# Revit family: 926-00-001-DN80-1800
name_source: partatom
category: Pipe Accessories
units: mm (PartAtom-declared; Revit-internal decimal feet)

## family parameters
Always vertical = Yes
Cut with Voids When Loaded = No
Part Type = Valve - Breaks Into
Round Connector Dimension = Use Diameter
Shared = No
Work Plane-Based = No

## types (33) — shared parameters
Description_ = AVK DBL. ECC. BUTTERFLY VALVE, FLANGED, AWWA SHORT, PN10/16
Search_table = 926-00-001-DN80-1800
URL_product_pages = https://www.avkvalves.com
zero-valued in all types: Default Elevation

## per-type parameters (varying)
- DN080_PN10/16: A=127 mm; B=110 mm; Body_T=8 mm  [stored 0.0262467 ft]; Body_end_shaft_R=60 mm; Body_rib_L=20 mm  [stored 0.0656168 ft]; Body_rib_W=12 mm  [stored 0.0393701 ft]; Body_shaft_R1=58 mm; Body_shaft_R2=16 mm  [stored 0.0524934 ft]; Body_shaft_R2_T=7 mm  [stored 0.0229659 ft]; Body_shaft_R3=21 mm  [stored 0.0688976 ft]; Body_shaft_R3_T=4 mm  [stored 0.0131234 ft]; Bore_R=40 mm; C=185 mm; D=9 mm  [stored 0.0295276 ft]; DN=80 mm; DN080_PN10/16=926-A10-12-020140100000; DN1000_PN10=926-A10-12-020140100000; DN1000_PN16=926-080-12-020140100000; DN100_PN10/16=926-100-12-020140100000; DN150_PN10/16=926-150-12-020040100000; DN200_PN10=926-200-12-010040100000; DN200_PN16=926-200-12-020040100000; DN250_PN10=926-250-12-010040100000; DN250_PN16=926-250-12-020040100000; DN300_PN10=926-300-12-010040100000; DN300_PN16=926-300-12-020040100000; DN350_PN10=926-350-12-010040100000; DN350_PN16=926-350-12-020040100000; DN400_PN10=926-400-12-010040100000; DN400_PN16=926-400-12-020040100000; DN500_PN10=926-500-12-010040100000; DN500_PN16=926-500-12-020040100000; DN600_PN10=926-600-12-020040100000; DN600_PN16=926-600-12-020040100000; DN700_PN10=926-700-12-020040100000; DN700_PN16=926-700-12-020040100000; E=18 mm  [stored 0.0590551 ft]; FL_R=72 mm; FL_T=8 mm  [stored 0.0262467 ft]; Hole_R=5 mm  [stored 0.0164042 ft]; L=3 mm  [stored 0.00984252 ft]; PCD=160 mm; Raised_R=66 mm; Raised_dis=2 mm  [stored 0.00656168 ft]; Retainer=16 mm  [stored 0.0524934 ft]; Rib_R=5 mm  [stored 0.0164042 ft]; Rib_T=4 mm  [stored 0.0131234 ft]; Rib_shaft=21 mm  [stored 0.0688976 ft]; Rib_shaft1=16 mm  [stored 0.0524934 ft]; Seal_R=16 mm  [stored 0.0524934 ft]; Slot_T=14 mm  [stored 0.0459318 ft]; Slot_dim1=15 mm  [stored 0.0492126 ft]; Slt=9 mm  [stored 0.0295276 ft]; Stem_R=7 mm  [stored 0.0229659 ft]; Top _Flange_dim1=12 mm  [stored 0.0393701 ft]; Top _Flange_dim2=8 mm  [stored 0.0262467 ft]; Top_Flange1=9 mm  [stored 0.0295276 ft]; Top_Flange_R=45 mm; Top_Flange_R_T=28 mm  [stored 0.0918635 ft]; Top_Flange_T=7 mm  [stored 0.0229659 ft]; Top_Rib=5 mm  [stored 0.0164042 ft]; Wedge=98 mm; bottom_Shaft_R=25 mm  [stored 0.082021 ft]; bottom_Shaft_T=5 mm  [stored 0.0164042 ft]; bottom_support_T=24 mm  [stored 0.0787402 ft]; logo=50 mm; rib_Loctn=8 mm  [stored 0.0262467 ft]; total_FL_legth=124 mm
- DN100_PN10/16: A=127 mm; B=130 mm; Body_T=10 mm  [stored 0.0328084 ft]; Body_end_shaft_R=60 mm; Body_rib_L=25 mm  [stored 0.082021 ft]; Body_rib_W=15 mm  [stored 0.0492126 ft]; Body_shaft_R1=58 mm; Body_shaft_R2=20 mm  [stored 0.0656168 ft]; Body_shaft_R2_T=9 mm  [stored 0.0295276 ft]; Body_shaft_R3=26 mm; Body_shaft_R3_T=5 mm  [stored 0.0164042 ft]; Bore_R=50 mm; C=202 mm; D=11 mm  [stored 0.0360892 ft]; DN=100 mm; DN080_PN10/16=926-080-00-020140100000; DN1000_PN10=926-A10-00-010020100000; DN1000_PN16=926-A10-00-020020100000; DN100_PN10/16=926-100-00-020140100000; DN1200_PN10=926-A12-00-010020100000; DN1200_PN16=926-A12-00-020020100000; DN1500_PN10=926-A15-00-010020100000; DN1500_PN16=926-A15-00-020020100000; DN150_PN10/16=926-150-00-020040100000; DN1800_PN10=926-A18-00-010020100000; DN1800_PN16=926-A18-00-020020100000; DN200_PN10=926-200-00-010040100000; DN200_PN16=926-200-00-020040100000; DN250_PN10=926-250-00-010040100000; DN250_PN16=926-250-00-020040100000; DN300_PN10=926-300-00-010040100000; DN300_PN16=926-300-00-020040100000; DN350_PN10=926-350-00-010040100000; DN350_PN16=926-350-00-020040100000; DN400_PN10=926-400-00-010040100000; DN400_PN16=926-400-00-020040100000; DN500_PN10=926-500-00-010040100000; DN500_PN16=926-500-00-020040100000; DN600_PN10=926-600-00-010040100000; DN600_PN16=926-600-00-020040100000; DN700_PN10=926-700-00-010020100000; DN700_PN16=926-700-00-020020100000; DN750_PN10=926-750-00-010020100000; DN750_PN16=926-750-00-020020100000; DN800_PN10=926-800-00-010020100000; DN800_PN16=926-800-00-020020100000; DN900_PN10=926-900-00-010020100000; DN900_PN16=926-900-00-020020100000; E=20 mm  [stored 0.0656168 ft]; FL_R=81 mm; FL_T=8 mm  [stored 0.0262467 ft]; Hole_R=6 mm  [stored 0.019685 ft]; L=3 mm  [stored 0.00984252 ft]; PCD=180 mm; Raised_R=78 mm; Raised_dis=2 mm  [stored 0.00656168 ft]; Retainer=16 mm  [stored 0.0524934 ft]; Rib_R=6 mm  [stored 0.019685 ft]; Rib_T=4 mm  [stored 0.0131234 ft]; Rib_shaft=26 mm; Rib_shaft1=20 mm  [stored 0.0656168 ft]; Seal_R=16 mm  [stored 0.0524934 ft]; Slot_T=14 mm  [stored 0.0459318 ft]; Slot_dim1=15 mm  [stored 0.0492126 ft]; Slt=11 mm  [stored 0.0360892 ft]; Stem_R=8 mm  [stored 0.0262467 ft]; Top _Flange_dim1=15 mm  [stored 0.0492126 ft]; Top _Flange_dim2=10 mm  [stored 0.0328084 ft]; Top_Flange1=15 mm  [stored 0.0492126 ft]; Top_Flange_R=63 mm; Top_Flange_R_T=28 mm  [stored 0.0918635 ft]; Top_Flange_T=9 mm  [stored 0.0295276 ft]; Top_Rib=6 mm  [stored 0.019685 ft]; Wedge=98 mm; bottom_Shaft_R=31 mm  [stored 0.101706 ft]; bottom_Shaft_T=6 mm  [stored 0.019685 ft]; bottom_support_T=30 mm  [stored 0.0984252 ft]; logo=62 mm; rib_Loctn=10 mm  [stored 0.0328084 ft]; total_FL_legth=124 mm
- DN200_PN10: A=152 mm; B=200 mm; Body_T=12 mm  [stored 0.0393701 ft]; Body_end_shaft_R=71 mm; Body_rib_L=52 mm; Body_rib_W=22 mm  [stored 0.0721785 ft]; Body_shaft_R1=64 mm; Body_shaft_R2=42 mm; Body_shaft_R2_T=18 mm  [stored 0.0590551 ft]; Body_shaft_R3=54 mm; Body_shaft_R3_T=10 mm  [stored 0.0328084 ft]; Bore_R=100 mm; C=320 mm; D=22 mm  [stored 0.0721785 ft]; DN=200 mm; DN080_PN10/16=926-080-00-020140100000; DN1000_PN10=926-A10-00-010020100000; DN1000_PN16=926-A10-00-020020100000; DN100_PN10/16=926-100-00-020140100000; DN1200_PN10=926-A12-00-010020100000; DN1200_PN16=926-A12-00-020020100000; DN1500_PN10=926-A15-00-010020100000; DN1500_PN16=926-A15-00-020020100000; DN150_PN10/16=926-150-00-020040100000; DN1800_PN10=926-A18-00-010020100000; DN1800_PN16=926-A18-00-020020100000; DN200_PN10=926-200-00-010040100000; DN200_PN16=926-200-00-020040100000; DN250_PN10=926-250-00-010040100000; DN250_PN16=926-250-00-020040100000; DN300_PN10=926-300-00-010040100000; DN300_PN16=926-300-00-020040100000; DN350_PN10=926-350-00-010040100000; DN350_PN16=926-350-00-020040100000; DN400_PN10=926-400-00-010040100000; DN400_PN16=926-400-00-020040100000; DN500_PN10=926-500-00-010040100000; DN500_PN16=926-500-00-020040100000; DN600_PN10=926-600-00-010040100000; DN600_PN16=926-600-00-020040100000; DN700_PN10=926-700-00-010020100000; DN700_PN16=926-700-00-020020100000; DN750_PN10=926-750-00-010020100000; DN750_PN16=926-750-00-020020100000; DN800_PN10=926-800-00-010020100000; DN800_PN16=926-800-00-020020100000; DN900_PN10=926-900-00-010020100000; DN900_PN16=926-900-00-020020100000; E=30 mm  [stored 0.0984252 ft]; FL_R=133 mm; FL_T=20 mm  [stored 0.0656168 ft]; Hole_R=12 mm  [stored 0.0393701 ft]; L=5 mm  [stored 0.0164042 ft]; PCD=295 mm; Raised_R=133 mm; Raised_dis=3 mm  [stored 0.00984252 ft]; Retainer=16 mm  [stored 0.0524934 ft]; Rib_R=11 mm  [stored 0.0360892 ft]; Rib_T=11 mm  [stored 0.0360892 ft]; Rib_shaft=54 mm; Rib_shaft1=42 mm; Seal_R=16 mm  [stored 0.0524934 ft]; Slot_T=20 mm  [stored 0.0656168 ft]; Slot_dim1=21 mm  [stored 0.0688976 ft]; Slt=22 mm  [stored 0.0721785 ft]; Stem_R=17 mm  [stored 0.0557743 ft]; Top _Flange_dim1=31 mm  [stored 0.101706 ft]; Top _Flange_dim2=20 mm  [stored 0.0656168 ft]; Top_Flange1=22 mm  [stored 0.0721785 ft]; Top_Flange_R=75 mm; Top_Flange_R_T=40 mm; Top_Flange_T=18 mm  [stored 0.0590551 ft]; Top_Rib=11 mm  [stored 0.0360892 ft]; Wedge=117 mm; bottom_Shaft_R=65 mm; bottom_Shaft_T=9 mm  [stored 0.0295276 ft]; bottom_support_T=62 mm; logo=114 mm; rib_Loctn=21 mm  [stored 0.0688976 ft]; total_FL_legth=148 mm
- DN150_PN10/16: A=127 mm; B=170 mm; Body_T=12 mm  [stored 0.0393701 ft]; Body_end_shaft_R=60 mm; Body_rib_L=32 mm  [stored 0.104987 ft]; Body_rib_W=20 mm  [stored 0.0656168 ft]; Body_shaft_R1=57 mm; Body_shaft_R2=26 mm; Body_shaft_R2_T=14 mm  [stored 0.0459318 ft]; Body_shaft_R3=33 mm  [stored 0.108268 ft]; Body_shaft_R3_T=7 mm  [stored 0.0229659 ft]; Bore_R=75 mm; C=280 mm; D=17 mm  [stored 0.0557743 ft]; DN=150 mm; DN080_PN10/16=926-080-00-020140100000; DN1000_PN10=926-A10-00-010020100000; DN1000_PN16=926-A10-00-020020100000; DN100_PN10/16=926-100-00-020140100000; DN1200_PN10=926-A12-00-010020100000; DN1200_PN16=926-A12-00-020020100000; DN1500_PN10=926-A15-00-010020100000; DN1500_PN16=926-A15-00-020020100000; DN150_PN10/16=926-150-00-020040100000; DN1800_PN10=926-A18-00-010020100000; DN1800_PN16=926-A18-00-020020100000; DN200_PN10=926-200-00-010040100000; DN200_PN16=926-200-00-020040100000; DN250_PN10=926-250-00-010040100000; DN250_PN16=926-250-00-020040100000; DN300_PN10=926-300-00-010040100000; DN300_PN16=926-300-00-020040100000; DN350_PN10=926-350-00-010040100000; DN350_PN16=926-350-00-020040100000; DN400_PN10=926-400-00-010040100000; DN400_PN16=926-400-00-020040100000; DN500_PN10=926-500-00-010040100000; DN500_PN16=926-500-00-020040100000; DN600_PN10=926-600-00-010040100000; DN600_PN16=926-600-00-020040100000; DN700_PN10=926-700-00-010020100000; DN700_PN16=926-700-00-020020100000; DN750_PN10=926-750-00-010020100000; DN750_PN16=926-750-00-020020100000; DN800_PN10=926-800-00-010020100000; DN800_PN16=926-800-00-020020100000; DN900_PN10=926-900-00-010020100000; DN900_PN16=926-900-00-020020100000; E=27 mm  [stored 0.0885827 ft]; FL_R=108 mm; FL_T=10 mm  [stored 0.0328084 ft]; Hole_R=8 mm  [stored 0.0262467 ft]; L=3 mm  [stored 0.00984252 ft]; PCD=240 mm; Raised_R=106 mm; Raised_dis=2 mm  [stored 0.00656168 ft]; Retainer=17 mm  [stored 0.0557743 ft]; Rib_R=9 mm  [stored 0.0295276 ft]; Rib_T=5 mm  [stored 0.0164042 ft]; Rib_shaft=33 mm  [stored 0.108268 ft]; Rib_shaft1=26 mm; Seal_R=17 mm  [stored 0.0557743 ft]; Slot_T=22 mm  [stored 0.0721785 ft]; Slot_dim1=18 mm  [stored 0.0590551 ft]; Slt=17 mm  [stored 0.0557743 ft]; Stem_R=13 mm  [stored 0.0426509 ft]; Top _Flange_dim1=19 mm  [stored 0.062336 ft]; Top _Flange_dim2=14 mm  [stored 0.0459318 ft]; Top_Flange1=18 mm  [stored 0.0590551 ft]; Top_Flange_R=63 mm; Top_Flange_R_T=44 mm; Top_Flange_T=14 mm  [stored 0.0459318 ft]; Top_Rib=9 mm  [stored 0.0295276 ft]; Wedge=98 mm; bottom_Shaft_R=40 mm; bottom_Shaft_T=8 mm  [stored 0.0262467 ft]; bottom_support_T=38 mm  [stored 0.124672 ft]; logo=89 mm; rib_Loctn=13 mm  [stored 0.0426509 ft]; total_FL_legth=124 mm
- DN200_PN16: A=152 mm; B=200 mm; Body_T=14 mm  [stored 0.0459318 ft]; Body_end_shaft_R=71 mm; Body_rib_L=52 mm; Body_rib_W=22 mm  [stored 0.0721785 ft]; Body_shaft_R1=64 mm; Body_shaft_R2=42 mm; Body_shaft_R2_T=18 mm  [stored 0.0590551 ft]; Body_shaft_R3=54 mm; Body_shaft_R3_T=10 mm  [stored 0.0328084 ft]; Bore_R=100 mm; C=320 mm; D=22 mm  [stored 0.0721785 ft]; DN=200 mm; DN080_PN10/16=926-080-00-020140100000; DN1000_PN10=926-A10-00-010020100000; DN1000_PN16=926-A10-00-020020100000; DN100_PN10/16=926-100-00-020140100000; DN1200_PN10=926-A12-00-010020100000; DN1200_PN16=926-A12-00-020020100000; DN1500_PN10=926-A15-00-010020100000; DN1500_PN16=926-A15-00-020020100000; DN150_PN10/16=926-150-00-020040100000; DN1800_PN10=926-A18-00-010020100000; DN1800_PN16=926-A18-00-020020100000; DN200_PN10=926-200-00-010040100000; DN200_PN16=926-200-00-020040100000; DN250_PN10=926-250-00-010040100000; DN250_PN16=926-250-00-020040100000; DN300_PN10=926-300-00-010040100000; DN300_PN16=926-300-00-020040100000; DN350_PN10=926-350-00-010040100000; DN350_PN16=926-350-00-020040100000; DN400_PN10=926-400-00-010040100000; DN400_PN16=926-400-00-020040100000; DN500_PN10=926-500-00-010040100000; DN500_PN16=926-500-00-020040100000; DN600_PN10=926-600-00-010040100000; DN600_PN16=926-600-00-020040100000; DN700_PN10=926-700-00-010020100000; DN700_PN16=926-700-00-020020100000; DN750_PN10=926-750-00-010020100000; DN750_PN16=926-750-00-020020100000; DN800_PN10=926-800-00-010020100000; DN800_PN16=926-800-00-020020100000; DN900_PN10=926-900-00-010020100000; DN900_PN16=926-900-00-020020100000; E=30 mm  [stored 0.0984252 ft]; FL_R=133 mm; FL_T=20 mm  [stored 0.0656168 ft]; Hole_R=12 mm  [stored 0.0393701 ft]; L=5 mm  [stored 0.0164042 ft]; PCD=295 mm; Raised_R=133 mm; Raised_dis=3 mm  [stored 0.00984252 ft]; Retainer=16 mm  [stored 0.0524934 ft]; Rib_R=11 mm  [stored 0.0360892 ft]; Rib_T=11 mm  [stored 0.0360892 ft]; Rib_shaft=54 mm; Rib_shaft1=42 mm; Seal_R=16 mm  [stored 0.0524934 ft]; Slot_T=20 mm  [stored 0.0656168 ft]; Slot_dim1=21 mm  [stored 0.0688976 ft]; Slt=22 mm  [stored 0.0721785 ft]; Stem_R=17 mm  [stored 0.0557743 ft]; Top _Flange_dim1=31 mm  [stored 0.101706 ft]; Top _Flange_dim2=20 mm  [stored 0.0656168 ft]; Top_Flange1=21 mm  [stored 0.0688976 ft]; Top_Flange_R=75 mm; Top_Flange_R_T=40 mm; Top_Flange_T=18 mm  [stored 0.0590551 ft]; Top_Rib=11 mm  [stored 0.0360892 ft]; Wedge=117 mm; bottom_Shaft_R=65 mm; bottom_Shaft_T=9 mm  [stored 0.0295276 ft]; bottom_support_T=62 mm; logo=116 mm; rib_Loctn=21 mm  [stored 0.0688976 ft]; total_FL_legth=148 mm
- DN250_PN10: A=203 mm; B=222 mm; Body_T=14 mm  [stored 0.0459318 ft]; Body_end_shaft_R=96 mm; Body_rib_L=56 mm; Body_rib_W=24 mm  [stored 0.0787402 ft]; Body_shaft_R1=88 mm; Body_shaft_R2=45 mm; Body_shaft_R2_T=22 mm  [stored 0.0721785 ft]; Body_shaft_R3=58 mm; Body_shaft_R3_T=12 mm  [stored 0.0393701 ft]; Bore_R=125 mm; C=340 mm; D=27 mm  [stored 0.0885827 ft]; DN=250 mm; DN080_PN10/16=926-080-00-020140100000; DN1000_PN10=926-A10-00-010020100000; DN1000_PN16=926-A10-00-020020100000; DN100_PN10/16=926-100-00-020140100000; DN1200_PN10=926-A12-00-010020100000; DN1200_PN16=926-A12-00-020020100000; DN1500_PN10=926-A15-00-010020100000; DN1500_PN16=926-A15-00-020020100000; DN150_PN10/16=926-150-00-020040100000; DN1800_PN10=926-A18-00-010020100000; DN1800_PN16=926-A18-00-020020100000; DN200_PN10=926-200-00-010040100000; DN200_PN16=926-200-00-020040100000; DN250_PN10=926-250-00-010040100000; DN250_PN16=926-250-00-020040100000; DN300_PN10=926-300-00-010040100000; DN300_PN16=926-300-00-020040100000; DN350_PN10=926-350-00-010040100000; DN350_PN16=926-350-00-020040100000; DN400_PN10=926-400-00-010040100000; DN400_PN16=926-400-00-020040100000; DN500_PN10=926-500-00-010040100000; DN500_PN16=926-500-00-020040100000; DN600_PN10=926-600-00-010040100000; DN600_PN16=926-600-00-020040100000; DN700_PN10=926-700-00-010020100000; DN700_PN16=926-700-00-020020100000; DN750_PN10=926-750-00-010020100000; DN750_PN16=926-750-00-020020100000; DN800_PN10=926-800-00-010020100000; DN800_PN16=926-800-00-020020100000; DN900_PN10=926-900-00-010020100000; DN900_PN16=926-900-00-020020100000; E=36 mm  [stored 0.11811 ft]; FL_R=158 mm; FL_T=22 mm  [stored 0.0721785 ft]; Hole_R=12 mm  [stored 0.0393701 ft]; L=5 mm  [stored 0.0164042 ft]; PCD=350 mm; Raised_R=160 mm; Raised_dis=3 mm  [stored 0.00984252 ft]; Retainer=16 mm  [stored 0.0524934 ft]; Rib_R=14 mm  [stored 0.0459318 ft]; Rib_T=13 mm  [stored 0.0426509 ft]; Rib_shaft=58 mm; Rib_shaft1=45 mm; Seal_R=16 mm  [stored 0.0524934 ft]; Slot_T=20 mm  [stored 0.0656168 ft]; Slot_dim1=6 mm  [stored 0.019685 ft]; Slt=27 mm  [stored 0.0885827 ft]; Stem_R=20 mm  [stored 0.0656168 ft]; Top _Flange_dim1=34 mm; Top _Flange_dim2=24 mm  [stored 0.0787402 ft]; Top_Flange1=21 mm  [stored 0.0688976 ft]; Top_Flange_R=75 mm; Top_Flange_R_T=40 mm; Top_Flange_T=22 mm  [stored 0.0721785 ft]; Top_Rib=14 mm  [stored 0.0459318 ft]; Wedge=156 mm; bottom_Shaft_R=70 mm; bottom_Shaft_T=10 mm  [stored 0.0328084 ft]; bottom_support_T=67 mm; logo=141 mm; rib_Loctn=22 mm  [stored 0.0721785 ft]; total_FL_legth=199 mm
- DN250_PN16: A=203 mm; B=222 mm; Body_T=4 mm  [stored 0.0131234 ft]; Body_end_shaft_R=96 mm; Body_rib_L=56 mm; Body_rib_W=24 mm  [stored 0.0787402 ft]; Body_shaft_R1=88 mm; Body_shaft_R2=45 mm; Body_shaft_R2_T=22 mm  [stored 0.0721785 ft]; Body_shaft_R3=58 mm; Body_shaft_R3_T=12 mm  [stored 0.0393701 ft]; Bore_R=125 mm; C=340 mm; D=27 mm  [stored 0.0885827 ft]; DN=250 mm; DN080_PN10/16=926-080-00-020140100000; DN1000_PN10=926-A10-00-010020100000; DN1000_PN16=926-A10-00-020020100000; DN100_PN10/16=926-100-00-020140100000; DN1200_PN10=926-A12-00-010020100000; DN1200_PN16=926-A12-00-020020100000; DN1500_PN10=926-A15-00-010020100000; DN1500_PN16=926-A15-00-020020100000; DN150_PN10/16=926-150-00-020040100000; DN1800_PN10=926-A18-00-010020100000; DN1800_PN16=926-A18-00-020020100000; DN200_PN10=926-200-00-010040100000; DN200_PN16=926-200-00-020040100000; DN250_PN10=926-250-00-010040100000; DN250_PN16=926-250-00-020040100000; DN300_PN10=926-300-00-010040100000; DN300_PN16=926-300-00-020040100000; DN350_PN10=926-350-00-010040100000; DN350_PN16=926-350-00-020040100000; DN400_PN10=926-400-00-010040100000; DN400_PN16=926-400-00-020040100000; DN500_PN10=926-500-00-010040100000; DN500_PN16=926-500-00-020040100000; DN600_PN10=926-600-00-010040100000; DN600_PN16=926-600-00-020040100000; DN700_PN10=926-700-00-010020100000; DN700_PN16=926-700-00-020020100000; DN750_PN10=926-750-00-010020100000; DN750_PN16=926-750-00-020020100000; DN800_PN10=926-800-00-010020100000; DN800_PN16=926-800-00-020020100000; DN900_PN10=926-900-00-010020100000; DN900_PN16=926-900-00-020020100000; E=36 mm  [stored 0.11811 ft]; FL_R=160 mm; FL_T=22 mm  [stored 0.0721785 ft]; Hole_R=11 mm  [stored 0.0360892 ft]; L=5 mm  [stored 0.0164042 ft]; PCD=355 mm; Raised_R=160 mm; Raised_dis=3 mm  [stored 0.00984252 ft]; Retainer=17 mm  [stored 0.0557743 ft]; Rib_R=14 mm  [stored 0.0459318 ft]; Rib_T=13 mm  [stored 0.0426509 ft]; Rib_shaft=58 mm; Rib_shaft1=45 mm; Seal_R=17 mm  [stored 0.0557743 ft]; Slot_T=20 mm  [stored 0.0656168 ft]; Slot_dim1=6 mm  [stored 0.019685 ft]; Slt=27 mm  [stored 0.0885827 ft]; Stem_R=20 mm  [stored 0.0656168 ft]; Top _Flange_dim1=34 mm; Top _Flange_dim2=24 mm  [stored 0.0787402 ft]; Top_Flange1=22 mm  [stored 0.0721785 ft]; Top_Flange_R=75 mm; Top_Flange_R_T=40 mm; Top_Flange_T=22 mm  [stored 0.0721785 ft]; Top_Rib=14 mm  [stored 0.0459318 ft]; Wedge=156 mm; bottom_Shaft_R=70 mm; bottom_Shaft_T=10 mm  [stored 0.0328084 ft]; bottom_support_T=67 mm; logo=131 mm; rib_Loctn=22 mm  [stored 0.0721785 ft]; total_FL_legth=199 mm
- DN300_PN10: A=203 mm; B=260 mm; Body_T=14 mm  [stored 0.0459318 ft]; Body_end_shaft_R=95 mm; Body_rib_L=60 mm; Body_rib_W=30 mm  [stored 0.0984252 ft]; Body_shaft_R1=86 mm; Body_shaft_R2=48 mm; Body_shaft_R2_T=22 mm  [stored 0.0721785 ft]; Body_shaft_R3=62 mm; Body_shaft_R3_T=12 mm  [stored 0.0393701 ft]; Bore_R=150 mm; C=390 mm; D=27 mm  [stored 0.0885827 ft]; DN=300 mm; DN080_PN10/16=926-080-00-020140100000; DN1000_PN10=926-A10-00-010020100000; DN1000_PN16=926-A10-00-020020100000; DN100_PN10/16=926-100-00-020140100000; DN1200_PN10=926-A12-00-010020100000; DN1200_PN16=926-A12-00-020020100000; DN1500_PN10=926-A15-00-010020100000; DN1500_PN16=926-A15-00-020020100000; DN150_PN10/16=926-150-00-020040100000; DN1800_PN10=926-A18-00-010020100000; DN1800_PN16=926-A18-00-020020100000; DN200_PN10=926-200-00-010040100000; DN200_PN16=926-200-00-020040100000; DN250_PN10=926-250-00-010040100000; DN250_PN16=926-250-00-020040100000; DN300_PN10=926-300-00-010040100000; DN300_PN16=926-300-00-020040100000; DN350_PN10=926-350-00-010040100000; DN350_PN16=926-350-00-020040100000; DN400_PN10=926-400-00-010040100000; DN400_PN16=926-400-00-020040100000; DN500_PN10=926-500-00-010040100000; DN500_PN16=926-500-00-020040100000; DN600_PN10=926-600-00-010040100000; DN600_PN16=926-600-00-020040100000; DN700_PN10=926-700-00-010020100000; DN700_PN16=926-700-00-020020100000; DN750_PN10=926-750-00-010020100000; DN750_PN16=926-750-00-020020100000; DN800_PN10=926-800-00-010020100000; DN800_PN16=926-800-00-020020100000; DN900_PN10=926-900-00-010020100000; DN900_PN16=926-900-00-020020100000; E=41 mm; FL_R=180 mm; FL_T=25 mm  [stored 0.082021 ft]; Hole_R=12 mm  [stored 0.0393701 ft]; L=6 mm  [stored 0.019685 ft]; PCD=400 mm; Raised_R=185 mm; Raised_dis=4 mm  [stored 0.0131234 ft]; Retainer=15 mm  [stored 0.0492126 ft]; Rib_R=14 mm  [stored 0.0459318 ft]; Rib_T=14 mm  [stored 0.0459318 ft]; Rib_shaft=52 mm; Rib_shaft1=48 mm; Seal_R=15 mm  [stored 0.0492126 ft]; Slot_T=20 mm  [stored 0.0656168 ft]; Slot_dim1=6 mm  [stored 0.019685 ft]; Slt=27 mm  [stored 0.0885827 ft]; Stem_R=20 mm  [stored 0.0656168 ft]; Top _Flange_dim1=36 mm  [stored 0.11811 ft]; Top _Flange_dim2=24 mm  [stored 0.0787402 ft]; Top_Flange1=22 mm  [stored 0.0721785 ft]; Top_Flange_R=75 mm; Top_Flange_R_T=40 mm; Top_Flange_T=22 mm  [stored 0.0721785 ft]; Top_Rib=14 mm  [stored 0.0459318 ft]; Wedge=156 mm; bottom_Shaft_R=75 mm; bottom_Shaft_T=12 mm  [stored 0.0393701 ft]; bottom_support_T=72 mm; logo=166 mm; rib_Loctn=24 mm  [stored 0.0787402 ft]; total_FL_legth=197 mm
- DN300_PN16: A=203 mm; B=260 mm; Body_T=14 mm  [stored 0.0459318 ft]; Body_end_shaft_R=95 mm; Body_rib_L=60 mm; Body_rib_W=30 mm  [stored 0.0984252 ft]; Body_shaft_R1=86 mm; Body_shaft_R2=48 mm; Body_shaft_R2_T=22 mm  [stored 0.0721785 ft]; Body_shaft_R3=62 mm; Body_shaft_R3_T=12 mm  [stored 0.0393701 ft]; Bore_R=150 mm; C=390 mm; D=27 mm  [stored 0.0885827 ft]; DN=300 mm; DN080_PN10/16=926-080-00-020140100000; DN1000_PN10=926-A10-00-010020100000; DN1000_PN16=926-A10-00-020020100000; DN100_PN10/16=926-100-00-020140100000; DN1200_PN10=926-A12-00-010020100000; DN1200_PN16=926-A12-00-020020100000; DN1500_PN10=926-A15-00-010020100000; DN1500_PN16=926-A15-00-020020100000; DN150_PN10/16=926-150-00-020040100000; DN1800_PN10=926-A18-00-010020100000; DN1800_PN16=926-A18-00-020020100000; DN200_PN10=926-200-00-010040100000; DN200_PN16=926-200-00-020040100000; DN250_PN10=926-250-00-010040100000; DN250_PN16=926-250-00-020040100000; DN300_PN10=926-300-00-010040100000; DN300_PN16=926-300-00-020040100000; DN350_PN10=926-350-00-010040100000; DN350_PN16=926-350-00-020040100000; DN400_PN10=926-400-00-010040100000; DN400_PN16=926-400-00-020040100000; DN500_PN10=926-500-00-010040100000; DN500_PN16=926-500-00-020040100000; DN600_PN10=926-600-00-010040100000; DN600_PN16=926-600-00-020040100000; DN700_PN10=926-700-00-010020100000; DN700_PN16=926-700-00-020020100000; DN750_PN10=926-750-00-010020100000; DN750_PN16=926-750-00-020020100000; DN800_PN10=926-800-00-010020100000; DN800_PN16=926-800-00-020020100000; DN900_PN10=926-900-00-010020100000; DN900_PN16=926-900-00-020020100000; E=41 mm; FL_R=185 mm; FL_T=25 mm  [stored 0.082021 ft]; Hole_R=12 mm  [stored 0.0393701 ft]; L=6 mm  [stored 0.019685 ft]; PCD=410 mm; Raised_R=185 mm; Raised_dis=4 mm  [stored 0.0131234 ft]; Retainer=17 mm  [stored 0.0557743 ft]; Rib_R=14 mm  [stored 0.0459318 ft]; Rib_T=14 mm  [stored 0.0459318 ft]; Rib_shaft=52 mm; Rib_shaft1=48 mm; Seal_R=17 mm  [stored 0.0557743 ft]; Slot_T=20 mm  [stored 0.0656168 ft]; Slot_dim1=6 mm  [stored 0.019685 ft]; Slt=27 mm  [stored 0.0885827 ft]; Stem_R=20 mm  [stored 0.0656168 ft]; Top _Flange_dim1=36 mm  [stored 0.11811 ft]; Top _Flange_dim2=24 mm  [stored 0.0787402 ft]; Top_Flange1=22 mm  [stored 0.0721785 ft]; Top_Flange_R=75 mm; Top_Flange_R_T=40 mm; Top_Flange_T=22 mm  [stored 0.0721785 ft]; Top_Rib=14 mm  [stored 0.0459318 ft]; Wedge=156 mm; bottom_Shaft_R=75 mm; bottom_Shaft_T=12 mm  [stored 0.0393701 ft]; bottom_support_T=72 mm; logo=166 mm; rib_Loctn=24 mm  [stored 0.0787402 ft]; total_FL_legth=197 mm
- DN400_PN16: A=203 mm; B=350 mm; Body_T=15 mm  [stored 0.0492126 ft]; Body_end_shaft_R=95 mm; Body_rib_L=70 mm; Body_rib_W=42 mm; Body_shaft_R1=85 mm; Body_shaft_R2=56 mm; Body_shaft_R2_T=29 mm  [stored 0.0951444 ft]; Body_shaft_R3=73 mm; Body_shaft_R3_T=16 mm  [stored 0.0524934 ft]; Bore_R=200 mm; C=451 mm; D=36 mm  [stored 0.11811 ft]; DN=400 mm; DN080_PN10/16=926-080-00-020140100000; DN1000_PN10=926-A10-00-010020100000; DN1000_PN16=926-A10-00-020020100000; DN100_PN10/16=926-100-00-020140100000; DN1200_PN10=926-A12-00-010020100000; DN1200_PN16=926-A12-00-020020100000; DN1500_PN10=926-A15-00-010020100000; DN1500_PN16=926-A15-00-020020100000; DN150_PN10/16=926-150-00-020040100000; DN1800_PN10=926-A18-00-010020100000; DN1800_PN16=926-A18-00-020020100000; DN200_PN10=926-200-00-010040100000; DN200_PN16=926-200-00-020040100000; DN250_PN10=926-250-00-010040100000; DN250_PN16=926-250-00-020040100000; DN300_PN10=926-300-00-010040100000; DN300_PN16=926-300-00-020040100000; DN350_PN10=926-350-00-010040100000; DN350_PN16=926-350-00-020040100000; DN400_PN10=926-400-00-010040100000; DN400_PN16=926-400-00-020040100000; DN500_PN10=926-500-00-010040100000; DN500_PN16=926-500-00-020040100000; DN600_PN10=926-600-00-010040100000; DN600_PN16=926-600-00-020040100000; DN700_PN10=926-700-00-010020100000; DN700_PN16=926-700-00-020020100000; DN750_PN10=926-750-00-010020100000; DN750_PN16=926-750-00-020020100000; DN800_PN10=926-800-00-010020100000; DN800_PN16=926-800-00-020020100000; DN900_PN10=926-900-00-010020100000; DN900_PN16=926-900-00-020020100000; E=41 mm; FL_R=236 mm; FL_T=28 mm  [stored 0.0918635 ft]; Hole_R=14 mm  [stored 0.0459318 ft]; L=6 mm  [stored 0.019685 ft]; PCD=510 mm; Raised_R=240 mm; Raised_dis=4 mm  [stored 0.0131234 ft]; Retainer=18 mm  [stored 0.0590551 ft]; Rib_R=18 mm  [stored 0.0590551 ft]; Rib_T=16 mm  [stored 0.0524934 ft]; Rib_shaft=73 mm; Rib_shaft1=50 mm; Seal_R=18 mm  [stored 0.0590551 ft]; Slot_T=22 mm  [stored 0.0721785 ft]; Slot_dim1=7 mm  [stored 0.0229659 ft]; Slt=36 mm  [stored 0.11811 ft]; Stem_R=27 mm  [stored 0.0885827 ft]; Top _Flange_dim1=42 mm; Top _Flange_dim2=32 mm  [stored 0.104987 ft]; Top_Flange1=29 mm  [stored 0.0951444 ft]; Top_Flange_R=105 mm; Top_Flange_R_T=44 mm; Top_Flange_T=29 mm  [stored 0.0951444 ft]; Top_Rib=18 mm  [stored 0.0590551 ft]; Wedge=156 mm; bottom_Shaft_R=87 mm; bottom_Shaft_T=17 mm  [stored 0.0557743 ft]; bottom_support_T=84 mm; logo=217 mm; rib_Loctn=28 mm  [stored 0.0918635 ft]; total_FL_legth=197 mm
- DN400_PN10: A=203 mm; B=350 mm; Body_T=15 mm  [stored 0.0492126 ft]; Body_end_shaft_R=95 mm; Body_rib_L=70 mm; Body_rib_W=42 mm; Body_shaft_R1=86 mm; Body_shaft_R2=56 mm; Body_shaft_R2_T=29 mm  [stored 0.0951444 ft]; Body_shaft_R3=73 mm; Body_shaft_R3_T=16 mm  [stored 0.0524934 ft]; Bore_R=200 mm; C=451 mm; D=36 mm  [stored 0.11811 ft]; DN=400 mm; DN080_PN10/16=926-080-00-020140100000; DN1000_PN10=926-A10-00-010020100000; DN1000_PN16=926-A10-00-020020100000; DN100_PN10/16=926-100-00-020140100000; DN1200_PN10=926-A12-00-010020100000; DN1200_PN16=926-A12-00-020020100000; DN1500_PN10=926-A15-00-010020100000; DN1500_PN16=926-A15-00-020020100000; DN150_PN10/16=926-150-00-020040100000; DN1800_PN10=926-A18-00-010020100000; DN1800_PN16=926-A18-00-020020100000; DN200_PN10=926-200-00-010040100000; DN200_PN16=926-200-00-020040100000; DN250_PN10=926-250-00-010040100000; DN250_PN16=926-250-00-020040100000; DN300_PN10=926-300-00-010040100000; DN300_PN16=926-300-00-020040100000; DN350_PN10=926-350-00-010040100000; DN350_PN16=926-350-00-020040100000; DN400_PN10=926-400-00-010040100000; DN400_PN16=926-400-00-020040100000; DN500_PN10=926-500-00-010040100000; DN500_PN16=926-500-00-020040100000; DN600_PN10=926-600-00-010040100000; DN600_PN16=926-600-00-020040100000; DN700_PN10=926-700-00-010020100000; DN700_PN16=926-700-00-020020100000; DN750_PN10=926-750-00-010020100000; DN750_PN16=926-750-00-020020100000; DN800_PN10=926-800-00-010020100000; DN800_PN16=926-800-00-020020100000; DN900_PN10=926-900-00-010020100000; DN900_PN16=926-900-00-020020100000; E=41 mm; FL_R=232 mm; FL_T=25 mm  [stored 0.082021 ft]; Hole_R=14 mm  [stored 0.0459318 ft]; L=6 mm  [stored 0.019685 ft]; PCD=510 mm; Raised_R=240 mm; Raised_dis=4 mm  [stored 0.0131234 ft]; Retainer=16 mm  [stored 0.0524934 ft]; Rib_R=18 mm  [stored 0.0590551 ft]; Rib_T=14 mm  [stored 0.0459318 ft]; Rib_shaft=73 mm; Rib_shaft1=50 mm; Seal_R=16 mm  [stored 0.0524934 ft]; Slot_T=22 mm  [stored 0.0721785 ft]; Slot_dim1=7 mm  [stored 0.0229659 ft]; Slt=36 mm  [stored 0.11811 ft]; Stem_R=27 mm  [stored 0.0885827 ft]; Top _Flange_dim1=42 mm; Top _Flange_dim2=32 mm  [stored 0.104987 ft]; Top_Flange1=29 mm  [stored 0.0951444 ft]; Top_Flange_R=105 mm; Top_Flange_R_T=44 mm; Top_Flange_T=29 mm  [stored 0.0951444 ft]; Top_Rib=18 mm  [stored 0.0590551 ft]; Wedge=156 mm; bottom_Shaft_R=87 mm; bottom_Shaft_T=17 mm  [stored 0.0557743 ft]; bottom_support_T=84 mm; logo=217 mm; rib_Loctn=28 mm  [stored 0.0918635 ft]; total_FL_legth=197 mm
- DN500_PN16: A=203 mm; B=380 mm; Body_T=3 mm  [stored 0.00984252 ft]; Body_end_shaft_R=95 mm; Body_rib_L=78 mm; Body_rib_W=41 mm; Body_shaft_R1=84 mm; Body_shaft_R2=62 mm; Body_shaft_R2_T=37 mm; Body_shaft_R3=81 mm; Body_shaft_R3_T=16 mm  [stored 0.0524934 ft]; Bore_R=250 mm; C=511 mm; D=46 mm; DN=500 mm; DN080_PN10/16=926-080-00-020140100000; DN1000_PN10=926-A10-00-010020100000; DN1000_PN16=926-A10-00-020020100000; DN100_PN10/16=926-100-00-020140100000; DN1200_PN10=926-A12-00-010020100000; DN1200_PN16=926-A12-00-020020100000; DN1500_PN10=926-A15-00-010020100000; DN1500_PN16=926-A15-00-020020100000; DN150_PN10/16=926-150-00-020040100000; DN1800_PN10=926-A18-00-010020100000; DN1800_PN16=926-A18-00-020020100000; DN200_PN10=926-200-00-010040100000; DN200_PN16=926-200-00-020040100000; DN250_PN10=926-250-00-010040100000; DN250_PN16=926-250-00-020040100000; DN300_PN10=926-300-00-010040100000; DN300_PN16=926-300-00-020040100000; DN350_PN10=926-350-00-010040100000; DN350_PN16=926-350-00-020040100000; DN400_PN10=926-400-00-010040100000; DN400_PN16=926-400-00-020040100000; DN500_PN10=926-500-00-010040100000; DN500_PN16=926-500-00-020040100000; DN600_PN10=926-600-00-010040100000; DN600_PN16=926-600-00-020040100000; DN700_PN10=926-700-00-010020100000; DN700_PN16=926-700-00-020020100000; DN750_PN10=926-750-00-010020100000; DN750_PN16=926-750-00-020020100000; DN800_PN10=926-800-00-010020100000; DN800_PN16=926-800-00-020020100000; DN900_PN10=926-900-00-010020100000; DN900_PN16=926-900-00-020020100000; E=65 mm; FL_R=275 mm; FL_T=30 mm  [stored 0.0984252 ft]; Hole_R=15 mm  [stored 0.0492126 ft]; L=6 mm  [stored 0.019685 ft]; PCD=585 mm; Raised_R=274 mm; Raised_dis=4 mm  [stored 0.0131234 ft]; Retainer=13 mm  [stored 0.0426509 ft]; Rib_R=23 mm  [stored 0.0754593 ft]; Rib_T=17 mm  [stored 0.0557743 ft]; Rib_shaft=81 mm; Rib_shaft1=62 mm; Seal_R=13 mm  [stored 0.0426509 ft]; Slot_T=22 mm  [stored 0.0721785 ft]; Slot_dim1=7 mm  [stored 0.0229659 ft]; Slt=46 mm; Stem_R=35 mm  [stored 0.114829 ft]; Top _Flange_dim1=47 mm; Top _Flange_dim2=32 mm  [stored 0.104987 ft]; Top_Flange1=37 mm; Top_Flange_R=105 mm; Top_Flange_R_T=44 mm; Top_Flange_T=37 mm; Top_Rib=23 mm  [stored 0.0754593 ft]; Wedge=156 mm; bottom_Shaft_R=97 mm; bottom_Shaft_T=16 mm  [stored 0.0524934 ft]; bottom_support_T=94 mm; logo=255 mm; rib_Loctn=31 mm  [stored 0.101706 ft]; total_FL_legth=197 mm
- DN600_PN10: A=203 mm; B=450 mm; Body_T=3 mm  [stored 0.00984252 ft]; Body_end_shaft_R=95 mm; Body_rib_L=87 mm; Body_rib_W=38 mm  [stored 0.124672 ft]; Body_shaft_R1=85 mm; Body_shaft_R2=70 mm; Body_shaft_R2_T=44 mm; Body_shaft_R3=90 mm; Body_shaft_R3_T=20 mm  [stored 0.0656168 ft]; Bore_R=300 mm; C=561 mm; D=55 mm; DN=600 mm; DN080_PN10/16=926-080-00-020140100000; DN1000_PN10=926-A10-00-010020100000; DN1000_PN16=926-A10-00-020020100000; DN100_PN10/16=926-100-00-020140100000; DN1200_PN10=926-A12-00-010020100000; DN1200_PN16=926-A12-00-020020100000; DN1500_PN10=926-A15-00-010020100000; DN1500_PN16=926-A15-00-020020100000; DN150_PN10/16=926-150-00-020040100000; DN1800_PN10=926-A18-00-010020100000; DN1800_PN16=926-A18-00-020020100000; DN200_PN10=926-200-00-010040100000; DN200_PN16=926-200-00-020040100000; DN250_PN10=926-250-00-010040100000; DN250_PN16=926-250-00-020040100000; DN300_PN10=926-300-00-010040100000; DN300_PN16=926-300-00-020040100000; DN350_PN10=926-350-00-010040100000; DN350_PN16=926-350-00-020040100000; DN400_PN10=926-400-00-010040100000; DN400_PN16=926-400-00-020040100000; DN500_PN10=926-500-00-010040100000; DN500_PN16=926-500-00-020040100000; DN600_PN10=926-600-00-010040100000; DN600_PN16=926-600-00-020040100000; DN700_PN10=926-700-00-010020100000; DN700_PN16=926-700-00-020020100000; DN750_PN10=926-750-00-010020100000; DN750_PN16=926-750-00-020020100000; DN800_PN10=926-800-00-010020100000; DN800_PN16=926-800-00-020020100000; DN900_PN10=926-900-00-010020100000; DN900_PN16=926-900-00-020020100000; E=70 mm; FL_R=325 mm; FL_T=27 mm  [stored 0.0885827 ft]; Hole_R=14 mm  [stored 0.0459318 ft]; L=6 mm  [stored 0.019685 ft]; PCD=620 mm; Raised_R=291 mm; Raised_dis=4 mm  [stored 0.0131234 ft]; Retainer=13 mm  [stored 0.0426509 ft]; Rib_R=28 mm  [stored 0.0918635 ft]; Rib_T=15 mm  [stored 0.0492126 ft]; Rib_shaft=90 mm; Rib_shaft1=70 mm; Seal_R=10 mm  [stored 0.0328084 ft]; Slot_T=22 mm  [stored 0.0721785 ft]; Slot_dim1=9 mm  [stored 0.0295276 ft]; Slt=55 mm; Stem_R=41 mm; Top _Flange_dim1=52 mm; Top _Flange_dim2=40 mm; Top_Flange1=44 mm; Top_Flange_R=150 mm; Top_Flange_R_T=44 mm; Top_Flange_T=44 mm; Top_Rib=28 mm  [stored 0.0918635 ft]; Wedge=156 mm; bottom_Shaft_R=109 mm; bottom_Shaft_T=15 mm  [stored 0.0492126 ft]; bottom_support_T=104 mm; logo=305 mm; rib_Loctn=35 mm  [stored 0.114829 ft]; total_FL_legth=197 mm
- DN600_PN16: A=203 mm; B=450 mm; Body_T=3 mm  [stored 0.00984252 ft]; Body_end_shaft_R=95 mm; Body_rib_L=87 mm; Body_rib_W=38 mm  [stored 0.124672 ft]; Body_shaft_R1=83 mm; Body_shaft_R2=70 mm; Body_shaft_R2_T=44 mm; Body_shaft_R3=90 mm; Body_shaft_R3_T=20 mm  [stored 0.0656168 ft]; Bore_R=300 mm; C=561 mm; D=55 mm; DN=600 mm; DN080_PN10/16=926-080-00-020140100000; DN1000_PN10=926-A10-00-010020100000; DN1000_PN16=926-A10-00-020020100000; DN100_PN10/16=926-100-00-020140100000; DN1200_PN10=926-A12-00-010020100000; DN1200_PN16=926-A12-00-020020100000; DN1500_PN10=926-A15-00-010020100000; DN1500_PN16=926-A15-00-020020100000; DN150_PN10/16=926-150-00-020040100000; DN1800_PN10=926-A18-00-010020100000; DN1800_PN16=926-A18-00-020020100000; DN200_PN10=926-200-00-010040100000; DN200_PN16=926-200-00-020040100000; DN250_PN10=926-250-00-010040100000; DN250_PN16=926-250-00-020040100000; DN300_PN10=926-300-00-010040100000; DN300_PN16=926-300-00-020040100000; DN350_PN10=926-350-00-010040100000; DN350_PN16=926-350-00-020040100000; DN400_PN10=926-400-00-010040100000; DN400_PN16=926-400-00-020040100000; DN500_PN10=926-500-00-010040100000; DN500_PN16=926-500-00-020040100000; DN600_PN10=926-600-00-010040100000; DN600_PN16=926-600-00-020040100000; DN700_PN10=926-700-00-010020100000; DN700_PN16=926-700-00-020020100000; DN750_PN10=926-750-00-010020100000; DN750_PN16=926-750-00-020020100000; DN800_PN10=926-800-00-010020100000; DN800_PN16=926-800-00-020020100000; DN900_PN10=926-900-00-010020100000; DN900_PN16=926-900-00-020020100000; E=70 mm; FL_R=330 mm; FL_T=32 mm  [stored 0.104987 ft]; Hole_R=16 mm  [stored 0.0524934 ft]; L=6 mm  [stored 0.019685 ft]; PCD=650 mm; Raised_R=305 mm; Raised_dis=4 mm  [stored 0.0131234 ft]; Retainer=15 mm  [stored 0.0492126 ft]; Rib_R=28 mm  [stored 0.0918635 ft]; Rib_T=18 mm  [stored 0.0590551 ft]; Rib_shaft=90 mm; Rib_shaft1=70 mm; Seal_R=10 mm  [stored 0.0328084 ft]; Slot_T=22 mm  [stored 0.0721785 ft]; Slot_dim1=9 mm  [stored 0.0295276 ft]; Slt=55 mm; Stem_R=41 mm; Top _Flange_dim1=52 mm; Top _Flange_dim2=40 mm; Top_Flange1=44 mm; Top_Flange_R=150 mm; Top_Flange_R_T=44 mm; Top_Flange_T=44 mm; Top_Rib=28 mm  [stored 0.0918635 ft]; Wedge=156 mm; bottom_Shaft_R=109 mm; bottom_Shaft_T=15 mm  [stored 0.0492126 ft]; bottom_support_T=104 mm; logo=305 mm; rib_Loctn=35 mm  [stored 0.114829 ft]; total_FL_legth=197 mm
- DN700_PN10: A=305 mm; B=500 mm; Body_T=3 mm  [stored 0.00984252 ft]; Body_end_shaft_R=144 mm; Body_rib_L=97 mm; Body_rib_W=45 mm; Body_shaft_R1=134 mm; Body_shaft_R2=78 mm; Body_shaft_R2_T=64 mm; Body_shaft_R3=101 mm; Body_shaft_R3_T=24 mm  [stored 0.0787402 ft]; Bore_R=350 mm; C=655 mm; D=80 mm; DN=700 mm; DN080_PN10/16=926-080-00-020140100000; DN1000_PN10=926-A10-00-010020100000; DN1000_PN16=926-A10-00-020020100000; DN100_PN10/16=926-100-00-020140100000; DN1200_PN10=926-A12-00-010020100000; DN1200_PN16=926-A12-00-020020100000; DN1500_PN10=926-A15-00-010020100000; DN1500_PN16=926-A15-00-020020100000; DN150_PN10/16=926-150-00-020040100000; DN1800_PN10=926-A18-00-010020100000; DN1800_PN16=926-A18-00-020020100000; DN200_PN10=926-200-00-010040100000; DN200_PN16=926-200-00-020040100000; DN250_PN10=926-250-00-010040100000; DN250_PN16=926-250-00-020040100000; DN300_PN10=926-300-00-010040100000; DN300_PN16=926-300-00-020040100000; DN350_PN10=926-350-00-010040100000; DN350_PN16=926-350-00-020040100000; DN400_PN10=926-400-00-010040100000; DN400_PN16=926-400-00-020040100000; DN500_PN10=926-500-00-010040100000; DN500_PN16=926-500-00-020040100000; DN600_PN10=926-600-00-010040100000; DN600_PN16=926-600-00-020040100000; DN700_PN10=926-700-00-010020100000; DN700_PN16=926-700-00-020020100000; DN750_PN10=926-750-00-010020100000; DN750_PN16=926-750-00-020020100000; DN800_PN10=926-800-00-010020100000; DN800_PN16=926-800-00-020020100000; DN900_PN10=926-900-00-010020100000; DN900_PN16=926-900-00-020020100000; E=110 mm; FL_R=375 mm; FL_T=30 mm  [stored 0.0984252 ft]; Hole_R=16 mm  [stored 0.0524934 ft]; L=8 mm  [stored 0.0262467 ft]; PCD=725 mm; Raised_R=341 mm; Raised_dis=5 mm  [stored 0.0164042 ft]; Retainer=13 mm  [stored 0.0426509 ft]; Rib_R=40 mm; Rib_T=17 mm  [stored 0.0557743 ft]; Rib_shaft=101 mm; Rib_shaft1=78 mm; Seal_R=10 mm  [stored 0.0328084 ft]; Slot_T=20 mm  [stored 0.0656168 ft]; Slot_dim1=11 mm  [stored 0.0360892 ft]; Slt=80 mm; Stem_R=60 mm; Top _Flange_dim1=59 mm; Top _Flange_dim2=48 mm; Top_Flange1=64 mm; Top_Flange_R=150 mm; Top_Flange_R_T=40 mm; Top_Flange_T=64 mm; Top_Rib=40 mm; Wedge=235 mm; bottom_Shaft_R=121 mm; bottom_Shaft_T=18 mm  [stored 0.0590551 ft]; bottom_support_T=116 mm; logo=355 mm; rib_Loctn=39 mm  [stored 0.127953 ft]; total_FL_legth=298 mm
- DN700_PN16: A=305 mm; B=500 mm; Body_T=3 mm  [stored 0.00984252 ft]; Body_end_shaft_R=144 mm; Body_rib_L=97 mm; Body_rib_W=30 mm  [stored 0.0984252 ft]; Body_shaft_R1=131 mm; Body_shaft_R2=78 mm; Body_shaft_R2_T=64 mm; Body_shaft_R3=101 mm; Body_shaft_R3_T=10 mm  [stored 0.0328084 ft]; Bore_R=350 mm; C=655 mm; D=80 mm; DN=700 mm; DN080_PN10/16=926-080-00-020140100000; DN1000_PN10=926-A10-00-010020100000; DN1000_PN16=926-A10-00-020020100000; DN100_PN10/16=926-100-00-020140100000; DN1200_PN10=926-A12-00-010020100000; DN1200_PN16=926-A12-00-020020100000; DN1500_PN10=926-A15-00-010020100000; DN1500_PN16=926-A15-00-020020100000; DN150_PN10/16=926-150-00-020040100000; DN1800_PN10=926-A18-00-010020100000; DN1800_PN16=926-A18-00-020020100000; DN200_PN10=926-200-00-010040100000; DN200_PN16=926-200-00-020040100000; DN250_PN10=926-250-00-010040100000; DN250_PN16=926-250-00-020040100000; DN300_PN10=926-300-00-010040100000; DN300_PN16=926-300-00-020040100000; DN350_PN10=926-350-00-010040100000; DN350_PN16=926-350-00-020040100000; DN400_PN10=926-400-00-010040100000; DN400_PN16=926-400-00-020040100000; DN500_PN10=926-500-00-010040100000; DN500_PN16=926-500-00-020040100000; DN600_PN10=926-600-00-010040100000; DN600_PN16=926-600-00-020040100000; DN700_PN10=926-700-00-010020100000; DN700_PN16=926-700-00-020020100000; DN750_PN10=926-750-00-010020100000; DN750_PN16=926-750-00-020020100000; DN800_PN10=926-800-00-010020100000; DN800_PN16=926-800-00-020020100000; DN900_PN10=926-900-00-010020100000; DN900_PN16=926-900-00-020020100000; E=110 mm; FL_R=375 mm; FL_T=36 mm  [stored 0.11811 ft]; Hole_R=16 mm  [stored 0.0524934 ft]; L=8 mm  [stored 0.0262467 ft]; PCD=750 mm; Raised_R=360 mm; Raised_dis=5 mm  [stored 0.0164042 ft]; Retainer=13 mm  [stored 0.0426509 ft]; Rib_R=40 mm; Rib_T=21 mm  [stored 0.0688976 ft]; Rib_shaft=101 mm; Rib_shaft1=78 mm; Seal_R=10 mm  [stored 0.0328084 ft]; Slot_T=20 mm  [stored 0.0656168 ft]; Slot_dim1=11 mm  [stored 0.0360892 ft]; Slt=80 mm; Stem_R=60 mm; Top _Flange_dim1=59 mm; Top _Flange_dim2=20 mm  [stored 0.0656168 ft]; Top_Flange1=64 mm; Top_Flange_R=150 mm; Top_Flange_R_T=40 mm; Top_Flange_T=140 mm; Top_Rib=40 mm; Wedge=235 mm; bottom_Shaft_R=121 mm; bottom_Shaft_T=12 mm  [stored 0.0393701 ft]; bottom_support_T=116 mm; logo=355 mm; rib_Loctn=39 mm  [stored 0.127953 ft]; total_FL_legth=298 mm
- DN750_PN10: A=305 mm; B=590 mm; Body_T=3 mm  [stored 0.00984252 ft]; Body_end_shaft_R=144 mm; Body_rib_L=105 mm; Body_rib_W=40 mm; Body_shaft_R1=129 mm; Body_shaft_R2=84 mm; Body_shaft_R2_T=64 mm; Body_shaft_R3=109 mm; Body_shaft_R3_T=35 mm  [stored 0.114829 ft]; Bore_R=375 mm; C=735 mm; D=80 mm; DN=750 mm; DN080_PN10/16=926-080-00-020140100000; DN1000_PN10=926-A10-00-010020100000; DN1000_PN16=926-A10-00-020020100000; DN100_PN10/16=926-100-00-020140100000; DN1200_PN10=926-A12-00-010020100000; DN1200_PN16=926-A12-00-020020100000; DN1500_PN10=926-A15-00-010020100000; DN1500_PN16=926-A15-00-020020100000; DN150_PN10/16=926-150-00-020040100000; DN1800_PN10=926-A18-00-010020100000; DN1800_PN16=926-A18-00-020020100000; DN200_PN10=926-200-00-010040100000; DN200_PN16=926-200-00-020040100000; DN250_PN10=926-250-00-010040100000; DN250_PN16=926-250-00-020040100000; DN300_PN10=926-300-00-010040100000; DN300_PN16=926-300-00-020040100000; DN350_PN10=926-350-00-010040100000; DN350_PN16=926-350-00-020040100000; DN400_PN10=926-400-00-010040100000; DN400_PN16=926-400-00-020040100000; DN500_PN10=926-500-00-010040100000; DN500_PN16=926-500-00-020040100000; DN600_PN10=926-600-00-010040100000; DN600_PN16=926-600-00-020040100000; DN700_PN10=926-700-00-010020100000; DN700_PN16=926-700-00-020020100000; DN750_PN10=926-750-00-010020100000; DN750_PN16=926-750-00-020020100000; DN800_PN10=926-800-00-010020100000; DN800_PN16=926-800-00-020020100000; DN900_PN10=926-900-00-010020100000; DN900_PN16=926-900-00-020020100000; E=110 mm; FL_R=420 mm; FL_T=40 mm; Hole_R=16 mm  [stored 0.0524934 ft]; L=8 mm  [stored 0.0262467 ft]; PCD=840 mm; Raised_R=397 mm; Raised_dis=5 mm  [stored 0.0164042 ft]; Retainer=23 mm  [stored 0.0754593 ft]; Rib_R=40 mm; Rib_T=23 mm  [stored 0.0754593 ft]; Rib_shaft=109 mm; Rib_shaft1=84 mm; Seal_R=10 mm  [stored 0.0328084 ft]; Slot_T=15 mm  [stored 0.0492126 ft]; Slot_dim1=16 mm  [stored 0.0524934 ft]; Slt=80 mm; Stem_R=60 mm; Top _Flange_dim1=63 mm; Top _Flange_dim2=70 mm; Top_Flange1=64 mm; Top_Flange_R=150 mm; Top_Flange_R_T=30 mm  [stored 0.0984252 ft]; Top_Flange_T=140 mm; Top_Rib=40 mm; Wedge=235 mm; bottom_Shaft_R=131 mm; bottom_Shaft_T=16 mm  [stored 0.0524934 ft]; bottom_support_T=126 mm; logo=380 mm; rib_Loctn=42 mm; total_FL_legth=298 mm
- DN750_PN16: A=305 mm; B=590 mm; Body_T=3 mm  [stored 0.00984252 ft]; Body_end_shaft_R=144 mm; Body_rib_L=105 mm; Body_rib_W=40 mm; Body_shaft_R1=129 mm; Body_shaft_R2=84 mm; Body_shaft_R2_T=64 mm; Body_shaft_R3=109 mm; Body_shaft_R3_T=35 mm  [stored 0.114829 ft]; Bore_R=375 mm; C=735 mm; D=80 mm; DN=750 mm; DN080_PN10/16=926-080-00-020140100000; DN1000_PN10=926-A10-00-010020100000; DN1000_PN16=926-A10-00-020020100000; DN100_PN10/16=926-100-00-020140100000; DN1200_PN10=926-A12-00-010020100000; DN1200_PN16=926-A12-00-020020100000; DN1500_PN10=926-A15-00-010020100000; DN1500_PN16=926-A15-00-020020100000; DN150_PN10/16=926-150-00-020040100000; DN1800_PN10=926-A18-00-010020100000; DN1800_PN16=926-A18-00-020020100000; DN200_PN10=926-200-00-010040100000; DN200_PN16=926-200-00-020040100000; DN250_PN10=926-250-00-010040100000; DN250_PN16=926-250-00-020040100000; DN300_PN10=926-300-00-010040100000; DN300_PN16=926-300-00-020040100000; DN350_PN10=926-350-00-010040100000; DN350_PN16=926-350-00-020040100000; DN400_PN10=926-400-00-010040100000; DN400_PN16=926-400-00-020040100000; DN500_PN10=926-500-00-010040100000; DN500_PN16=926-500-00-020040100000; DN600_PN10=926-600-00-010040100000; DN600_PN16=926-600-00-020040100000; DN700_PN10=926-700-00-010020100000; DN700_PN16=926-700-00-020020100000; DN750_PN10=926-750-00-010020100000; DN750_PN16=926-750-00-020020100000; DN800_PN10=926-800-00-010020100000; DN800_PN16=926-800-00-020020100000; DN900_PN10=926-900-00-010020100000; DN900_PN16=926-900-00-020020100000; E=110 mm; FL_R=420 mm; FL_T=40 mm; Hole_R=16 mm  [stored 0.0524934 ft]; L=8 mm  [stored 0.0262467 ft]; PCD=840 mm; Raised_R=397 mm; Raised_dis=5 mm  [stored 0.0164042 ft]; Retainer=23 mm  [stored 0.0754593 ft]; Rib_R=40 mm; Rib_T=23 mm  [stored 0.0754593 ft]; Rib_shaft=109 mm; Rib_shaft1=84 mm; Seal_R=10 mm  [stored 0.0328084 ft]; Slot_T=15 mm  [stored 0.0492126 ft]; Slot_dim1=16 mm  [stored 0.0524934 ft]; Slt=80 mm; Stem_R=60 mm; Top _Flange_dim1=63 mm; Top _Flange_dim2=70 mm; Top_Flange1=64 mm; Top_Flange_R=150 mm; Top_Flange_R_T=30 mm  [stored 0.0984252 ft]; Top_Flange_T=140 mm; Top_Rib=40 mm; Wedge=235 mm; bottom_Shaft_R=131 mm; bottom_Shaft_T=16 mm  [stored 0.0524934 ft]; bottom_support_T=126 mm; logo=380 mm; rib_Loctn=42 mm; total_FL_legth=298 mm
- DN800_PN10: A=305 mm; B=600 mm; Body_T=3 mm  [stored 0.00984252 ft]; Body_end_shaft_R=144 mm; Body_rib_L=115 mm; Body_rib_W=5 mm  [stored 0.0164042 ft]; Body_shaft_R1=129 mm; Body_shaft_R2=92 mm; Body_shaft_R2_T=64 mm; Body_shaft_R3=120 mm; Body_shaft_R3_T=1 mm  [stored 0.00328084 ft]; Bore_R=400 mm; C=740 mm; D=80 mm; DN=800 mm; DN080_PN10/16=926-080-00-020140100000; DN1000_PN10=926-A10-00-010020100000; DN1000_PN16=926-A10-00-020020100000; DN100_PN10/16=926-100-00-020140100000; DN1200_PN10=926-A12-00-010020100000; DN1200_PN16=926-A12-00-020020100000; DN1500_PN10=926-A15-00-010020100000; DN1500_PN16=926-A15-00-020020100000; DN150_PN10/16=926-150-00-020040100000; DN1800_PN10=926-A18-00-010020100000; DN1800_PN16=926-A18-00-020020100000; DN200_PN10=926-200-00-010040100000; DN200_PN16=926-200-00-020040100000; DN250_PN10=926-250-00-010040100000; DN250_PN16=926-250-00-020040100000; DN300_PN10=926-300-00-010040100000; DN300_PN16=926-300-00-020040100000; DN350_PN10=926-350-00-010040100000; DN350_PN16=926-350-00-020040100000; DN400_PN10=926-400-00-010040100000; DN400_PN16=926-400-00-020040100000; DN500_PN10=926-500-00-010040100000; DN500_PN16=926-500-00-020040100000; DN600_PN10=926-600-00-010040100000; DN600_PN16=926-600-00-020040100000; DN700_PN10=926-700-00-010020100000; DN700_PN16=926-700-00-020020100000; DN750_PN10=926-750-00-010020100000; DN750_PN16=926-750-00-020020100000; DN800_PN10=926-800-00-010020100000; DN800_PN16=926-800-00-020020100000; DN900_PN10=926-900-00-010020100000; DN900_PN16=926-900-00-020020100000; E=110 mm; FL_R=450 mm; FL_T=40 mm; Hole_R=19 mm  [stored 0.062336 ft]; L=8 mm  [stored 0.0262467 ft]; PCD=1050 mm; Raised_R=556 mm; Raised_dis=5 mm  [stored 0.0164042 ft]; Retainer=25 mm  [stored 0.082021 ft]; Rib_R=40 mm; Rib_T=23 mm  [stored 0.0754593 ft]; Rib_shaft=120 mm; Rib_shaft1=92 mm; Seal_R=61 mm; Slot_T=22 mm  [stored 0.0721785 ft]; Slot_dim1=15 mm  [stored 0.0492126 ft]; Slt=80 mm; Stem_R=60 mm; Top _Flange_dim1=69 mm; Top _Flange_dim2=2 mm  [stored 0.00656168 ft]; Top_Flange1=64 mm; Top_Flange_R=150 mm; Top_Flange_R_T=44 mm; Top_Flange_T=140 mm; Top_Rib=40 mm; Wedge=235 mm; bottom_Shaft_R=144 mm; bottom_Shaft_T=2 mm  [stored 0.00656168 ft]; bottom_support_T=138 mm; logo=405 mm; rib_Loctn=46 mm; total_FL_legth=298 mm
- DN800_PN16: A=305 mm; B=600 mm; Body_T=3 mm  [stored 0.00984252 ft]; Body_end_shaft_R=144 mm; Body_rib_L=115 mm; Body_rib_W=5 mm  [stored 0.0164042 ft]; Body_shaft_R1=124 mm; Body_shaft_R2=92 mm; Body_shaft_R2_T=64 mm; Body_shaft_R3=120 mm; Body_shaft_R3_T=1 mm  [stored 0.00328084 ft]; Bore_R=400 mm; C=740 mm; D=80 mm; DN=800 mm; DN080_PN10/16=926-080-00-020140100000; DN1000_PN10=926-A10-00-010020100000; DN1000_PN16=926-A10-00-020020100000; DN100_PN10/16=926-100-00-020140100000; DN1200_PN10=926-A12-00-010020100000; DN1200_PN16=926-A12-00-020020100000; DN1500_PN10=926-A15-00-010020100000; DN1500_PN16=926-A15-00-020020100000; DN150_PN10/16=926-150-00-020040100000; DN1800_PN10=926-A18-00-010020100000; DN1800_PN16=926-A18-00-020020100000; DN200_PN10=926-200-00-010040100000; DN200_PN16=926-200-00-020040100000; DN250_PN10=926-250-00-010040100000; DN250_PN16=926-250-00-020040100000; DN300_PN10=926-300-00-010040100000; DN300_PN16=926-300-00-020040100000; DN350_PN10=926-350-00-010040100000; DN350_PN16=926-350-00-020040100000; DN400_PN10=926-400-00-010040100000; DN400_PN16=926-400-00-020040100000; DN500_PN10=926-500-00-010040100000; DN500_PN16=926-500-00-020040100000; DN600_PN10=926-600-00-010040100000; DN600_PN16=926-600-00-020040100000; DN700_PN10=926-700-00-010020100000; DN700_PN16=926-700-00-020020100000; DN750_PN10=926-750-00-010020100000; DN750_PN16=926-750-00-020020100000; DN800_PN10=926-800-00-010020100000; DN800_PN16=926-800-00-020020100000; DN900_PN10=926-900-00-010020100000; DN900_PN16=926-900-00-020020100000; E=110 mm; FL_R=450 mm; FL_T=50 mm; Hole_R=19 mm  [stored 0.062336 ft]; L=8 mm  [stored 0.0262467 ft]; PCD=1050 mm; Raised_R=556 mm; Raised_dis=5 mm  [stored 0.0164042 ft]; Retainer=25 mm  [stored 0.082021 ft]; Rib_R=40 mm; Rib_T=30 mm  [stored 0.0984252 ft]; Rib_shaft=120 mm; Rib_shaft1=92 mm; Seal_R=63 mm; Slot_T=22 mm  [stored 0.0721785 ft]; Slot_dim1=15 mm  [stored 0.0492126 ft]; Slt=80 mm; Stem_R=60 mm; Top _Flange_dim1=69 mm; Top _Flange_dim2=2 mm  [stored 0.00656168 ft]; Top_Flange1=64 mm; Top_Flange_R=150 mm; Top_Flange_R_T=44 mm; Top_Flange_T=120 mm; Top_Rib=40 mm; Wedge=235 mm; bottom_Shaft_R=144 mm; bottom_Shaft_T=2 mm  [stored 0.00656168 ft]; bottom_support_T=138 mm; logo=405 mm; rib_Loctn=46 mm; total_FL_legth=298 mm
- DN900_PN10: A=305 mm; B=620 mm; Body_T=3 mm  [stored 0.00984252 ft]; Body_end_shaft_R=144 mm; Body_rib_L=115 mm; Body_rib_W=1 mm  [stored 0.00328084 ft]; Body_shaft_R1=129 mm; Body_shaft_R2=92 mm; Body_shaft_R2_T=60 mm; Body_shaft_R3=120 mm; Body_shaft_R3_T=33 mm  [stored 0.108268 ft]; Bore_R=450 mm; C=802 mm; D=75 mm; DN=900 mm; DN080_PN10/16=926-080-00-020140100000; DN1000_PN10=926-A10-00-010020100000; DN1000_PN16=926-A10-00-020020100000; DN100_PN10/16=926-100-00-020140100000; DN1200_PN10=926-A12-00-010020100000; DN1200_PN16=926-A12-00-020020100000; DN1500_PN10=926-A15-00-010020100000; DN1500_PN16=926-A15-00-020020100000; DN150_PN10/16=926-150-00-020040100000; DN1800_PN10=926-A18-00-010020100000; DN1800_PN16=926-A18-00-020020100000; DN200_PN10=926-200-00-010040100000; DN200_PN16=926-200-00-020040100000; DN250_PN10=926-250-00-010040100000; DN250_PN16=926-250-00-020040100000; DN300_PN10=926-300-00-010040100000; DN300_PN16=926-300-00-020040100000; DN350_PN10=926-350-00-010040100000; DN350_PN16=926-350-00-020040100000; DN400_PN10=926-400-00-010040100000; DN400_PN16=926-400-00-020040100000; DN500_PN10=926-500-00-010040100000; DN500_PN16=926-500-00-020040100000; DN600_PN10=926-600-00-010040100000; DN600_PN16=926-600-00-020040100000; DN700_PN10=926-700-00-010020100000; DN700_PN16=926-700-00-020020100000; DN750_PN10=926-750-00-010020100000; DN750_PN16=926-750-00-020020100000; DN800_PN10=926-800-00-010020100000; DN800_PN16=926-800-00-020020100000; DN900_PN10=926-900-00-010020100000; DN900_PN16=926-900-00-020020100000; E=108 mm; FL_R=515 mm; FL_T=40 mm; Hole_R=19 mm  [stored 0.062336 ft]; L=8 mm  [stored 0.0262467 ft]; PCD=1135 mm; Raised_R=556 mm; Raised_dis=5 mm  [stored 0.0164042 ft]; Retainer=33 mm  [stored 0.108268 ft]; Rib_R=38 mm  [stored 0.124672 ft]; Rib_T=23 mm  [stored 0.0754593 ft]; Rib_shaft=120 mm; Rib_shaft1=92 mm; Seal_R=36 mm  [stored 0.11811 ft]; Slot_T=22 mm  [stored 0.0721785 ft]; Slot_dim1=15 mm  [stored 0.0492126 ft]; Slt=75 mm; Stem_R=56 mm; Top _Flange_dim1=69 mm; Top _Flange_dim2=66 mm; Top_Flange1=60 mm; Top_Flange_R=175 mm; Top_Flange_R_T=44 mm; Top_Flange_T=120 mm; Top_Rib=38 mm  [stored 0.124672 ft]; Wedge=235 mm; bottom_Shaft_R=144 mm; bottom_Shaft_T=0 mm  [stored 0 ft]; bottom_support_T=138 mm; logo=455 mm; rib_Loctn=46 mm; total_FL_legth=298 mm
- DN900_PN16: A=305 mm; B=620 mm; Body_T=3 mm  [stored 0.00984252 ft]; Body_end_shaft_R=144 mm; Body_rib_L=115 mm; Body_rib_W=1 mm  [stored 0.00328084 ft]; Body_shaft_R1=124 mm; Body_shaft_R2=92 mm; Body_shaft_R2_T=60 mm; Body_shaft_R3=120 mm; Body_shaft_R3_T=33 mm  [stored 0.108268 ft]; Bore_R=450 mm; C=802 mm; D=75 mm; DN=900 mm; DN080_PN10/16=926-080-00-020140100000; DN1000_PN10=926-A10-00-010020100000; DN1000_PN16=926-A10-00-020020100000; DN100_PN10/16=926-100-00-020140100000; DN1200_PN10=926-A12-00-010020100000; DN1200_PN16=926-A12-00-020020100000; DN1500_PN10=926-A15-00-010020100000; DN1500_PN16=926-A15-00-020020100000; DN150_PN10/16=926-150-00-020040100000; DN1800_PN10=926-A18-00-010020100000; DN1800_PN16=926-A18-00-020020100000; DN200_PN10=926-200-00-010040100000; DN200_PN16=926-200-00-020040100000; DN250_PN10=926-250-00-010040100000; DN250_PN16=926-250-00-020040100000; DN300_PN10=926-300-00-010040100000; DN300_PN16=926-300-00-020040100000; DN350_PN10=926-350-00-010040100000; DN350_PN16=926-350-00-020040100000; DN400_PN10=926-400-00-010040100000; DN400_PN16=926-400-00-020040100000; DN500_PN10=926-500-00-010040100000; DN500_PN16=926-500-00-020040100000; DN600_PN10=926-600-00-010040100000; DN600_PN16=926-600-00-020040100000; DN700_PN10=926-700-00-010020100000; DN700_PN16=926-700-00-020020100000; DN750_PN10=926-750-00-010020100000; DN750_PN16=926-750-00-020020100000; DN800_PN10=926-800-00-010020100000; DN800_PN16=926-800-00-020020100000; DN900_PN10=926-900-00-010020100000; DN900_PN16=926-900-00-020020100000; E=108 mm; FL_R=520 mm; FL_T=50 mm; Hole_R=19 mm  [stored 0.062336 ft]; L=8 mm  [stored 0.0262467 ft]; PCD=1135 mm; Raised_R=556 mm; Raised_dis=5 mm  [stored 0.0164042 ft]; Retainer=35 mm  [stored 0.114829 ft]; Rib_R=38 mm  [stored 0.124672 ft]; Rib_T=30 mm  [stored 0.0984252 ft]; Rib_shaft=120 mm; Rib_shaft1=92 mm; Seal_R=38 mm  [stored 0.124672 ft]; Slot_T=22 mm  [stored 0.0721785 ft]; Slot_dim1=15 mm  [stored 0.0492126 ft]; Slt=75 mm; Stem_R=56 mm; Top _Flange_dim1=69 mm; Top _Flange_dim2=66 mm; Top_Flange1=60 mm; Top_Flange_R=175 mm; Top_Flange_R_T=44 mm; Top_Flange_T=75 mm; Top_Rib=38 mm  [stored 0.124672 ft]; Wedge=235 mm; bottom_Shaft_R=144 mm; bottom_Shaft_T=0 mm  [stored 0 ft]; bottom_support_T=138 mm; logo=455 mm; rib_Loctn=46 mm; total_FL_legth=298 mm
- DN1000_PN10: A=305 mm; B=700 mm; Body_T=3 mm  [stored 0.00984252 ft]; Body_end_shaft_R=144 mm; Body_rib_L=115 mm; Body_rib_W=33 mm  [stored 0.108268 ft]; Body_shaft_R1=129 mm; Body_shaft_R2=92 mm; Body_shaft_R2_T=60 mm; Body_shaft_R3=120 mm; Body_shaft_R3_T=33 mm  [stored 0.108268 ft]; Bore_R=500 mm; C=856 mm; D=75 mm; DN=1000 mm; DN080_PN10/16=926-080-00-020140100000; DN1000_PN10=926-A10-00-010020100000; DN1000_PN16=926-A10-00-020020100000; DN100_PN10/16=926-100-00-020140100000; DN1200_PN10=926-A12-00-010020100000; DN1200_PN16=926-A12-00-020020100000; DN1500_PN10=926-A15-00-010020100000; DN1500_PN16=926-A15-00-020020100000; DN150_PN10/16=926-150-00-020040100000; DN1800_PN10=926-A18-00-010020100000; DN1800_PN16=926-A18-00-020020100000; DN200_PN10=926-200-00-010040100000; DN200_PN16=926-200-00-020040100000; DN250_PN10=926-250-00-010040100000; DN250_PN16=926-250-00-020040100000; DN300_PN10=926-300-00-010040100000; DN300_PN16=926-300-00-020040100000; DN350_PN10=926-350-00-010040100000; DN350_PN16=926-350-00-020040100000; DN400_PN10=926-400-00-010040100000; DN400_PN16=926-400-00-020040100000; DN500_PN10=926-500-00-010040100000; DN500_PN16=926-500-00-020040100000; DN600_PN10=926-600-00-010040100000; DN600_PN16=926-600-00-020040100000; DN700_PN10=926-700-00-010020100000; DN700_PN16=926-700-00-020020100000; DN750_PN10=926-750-00-010020100000; DN750_PN16=926-750-00-020020100000; DN800_PN10=926-800-00-010020100000; DN800_PN16=926-800-00-020020100000; DN900_PN10=926-900-00-010020100000; DN900_PN16=926-900-00-020020100000; E=80 mm; FL_R=550 mm; FL_T=40 mm; Hole_R=19 mm  [stored 0.062336 ft]; L=8 mm  [stored 0.0262467 ft]; PCD=1160 mm; Raised_R=556 mm; Raised_dis=5 mm  [stored 0.0164042 ft]; Retainer=25 mm  [stored 0.082021 ft]; Rib_R=38 mm  [stored 0.124672 ft]; Rib_T=23 mm  [stored 0.0754593 ft]; Rib_shaft=120 mm; Rib_shaft1=92 mm; Seal_R=11 mm  [stored 0.0360892 ft]; Slot_T=22 mm  [stored 0.0721785 ft]; Slot_dim1=15 mm  [stored 0.0492126 ft]; Slt=75 mm; Stem_R=56 mm; Top _Flange_dim1=69 mm; Top _Flange_dim2=66 mm; Top_Flange1=60 mm; Top_Flange_R=175 mm; Top_Flange_R_T=44 mm; Top_Flange_T=75 mm; Top_Rib=38 mm  [stored 0.124672 ft]; Wedge=235 mm; bottom_Shaft_R=144 mm; bottom_Shaft_T=13 mm  [stored 0.0426509 ft]; bottom_support_T=138 mm; logo=505 mm; rib_Loctn=46 mm; total_FL_legth=298 mm
- DN1000_PN16: A=305 mm; B=700 mm; Body_T=3 mm  [stored 0.00984252 ft]; Body_end_shaft_R=144 mm; Body_rib_L=115 mm; Body_rib_W=33 mm  [stored 0.108268 ft]; Body_shaft_R1=124 mm; Body_shaft_R2=92 mm; Body_shaft_R2_T=60 mm; Body_shaft_R3=120 mm; Body_shaft_R3_T=33 mm  [stored 0.108268 ft]; Bore_R=500 mm; C=856 mm; D=75 mm; DN=1000 mm; DN080_PN10/16=926-080-00-020140100000; DN1000_PN10=926-A10-00-010020100000; DN1000_PN16=926-A10-00-020020100000; DN100_PN10/16=926-100-00-020140100000; DN1200_PN10=926-A12-00-010020100000; DN1200_PN16=926-A12-00-020020100000; DN1500_PN10=926-A15-00-010020100000; DN1500_PN16=926-A15-00-020020100000; DN150_PN10/16=926-150-00-020040100000; DN1800_PN10=926-A18-00-010020100000; DN1800_PN16=926-A18-00-020020100000; DN200_PN10=926-200-00-010040100000; DN200_PN16=926-200-00-020040100000; DN250_PN10=926-250-00-010040100000; DN250_PN16=926-250-00-020040100000; DN300_PN10=926-300-00-010040100000; DN300_PN16=926-300-00-020040100000; DN350_PN10=926-350-00-010040100000; DN350_PN16=926-350-00-020040100000; DN400_PN10=926-400-00-010040100000; DN400_PN16=926-400-00-020040100000; DN500_PN10=926-500-00-010040100000; DN500_PN16=926-500-00-020040100000; DN600_PN10=926-600-00-010040100000; DN600_PN16=926-600-00-020040100000; DN700_PN10=926-700-00-010020100000; DN700_PN16=926-700-00-020020100000; DN750_PN10=926-750-00-010020100000; DN750_PN16=926-750-00-020020100000; DN800_PN10=926-800-00-010020100000; DN800_PN16=926-800-00-020020100000; DN900_PN10=926-900-00-010020100000; DN900_PN16=926-900-00-020020100000; E=80 mm; FL_R=550 mm; FL_T=50 mm; Hole_R=19 mm  [stored 0.062336 ft]; L=8 mm  [stored 0.0262467 ft]; PCD=1170 mm; Raised_R=556 mm; Raised_dis=5 mm  [stored 0.0164042 ft]; Retainer=25 mm  [stored 0.082021 ft]; Rib_R=38 mm  [stored 0.124672 ft]; Rib_T=30 mm  [stored 0.0984252 ft]; Rib_shaft=120 mm; Rib_shaft1=92 mm; Seal_R=13 mm  [stored 0.0426509 ft]; Slot_T=22 mm  [stored 0.0721785 ft]; Slot_dim1=15 mm  [stored 0.0492126 ft]; Slt=75 mm; Stem_R=56 mm; Top _Flange_dim1=69 mm; Top _Flange_dim2=66 mm; Top_Flange1=60 mm; Top_Flange_R=175 mm; Top_Flange_R_T=44 mm; Top_Flange_T=75 mm; Top_Rib=38 mm  [stored 0.124672 ft]; Wedge=235 mm; bottom_Shaft_R=144 mm; bottom_Shaft_T=13 mm  [stored 0.0426509 ft]; bottom_support_T=138 mm; logo=505 mm; rib_Loctn=46 mm; total_FL_legth=298 mm
- DN1200_PN10: A=381 mm; B=850 mm; Body_T=3 mm  [stored 0.00984252 ft]; Body_end_shaft_R=182 mm; Body_rib_L=120 mm; Body_rib_W=60 mm; Body_shaft_R1=167 mm; Body_shaft_R2=96 mm; Body_shaft_R2_T=114 mm; Body_shaft_R3=125 mm; Body_shaft_R3_T=33 mm  [stored 0.108268 ft]; Bore_R=600 mm; C=1080 mm; D=143 mm; DN=1200 mm; DN080_PN10/16=926-080-00-020140100000; DN1000_PN10=926-A10-00-010020100000; DN1000_PN16=926-A10-00-020020100000; DN100_PN10/16=926-100-00-020140100000; DN1200_PN10=926-A12-00-010020100000; DN1200_PN16=926-A12-00-020020100000; DN1500_PN10=926-A15-00-010020100000; DN1500_PN16=926-A15-00-020020100000; DN150_PN10/16=926-150-00-020040100000; DN1800_PN10=926-A18-00-010020100000; DN1800_PN16=926-A18-00-020020100000; DN200_PN10=926-200-00-010040100000; DN200_PN16=926-200-00-020040100000; DN250_PN10=926-250-00-010040100000; DN250_PN16=926-250-00-020040100000; DN300_PN10=926-300-00-010040100000; DN300_PN16=926-300-00-020040100000; DN350_PN10=926-350-00-010040100000; DN350_PN16=926-350-00-020040100000; DN400_PN10=926-400-00-010040100000; DN400_PN16=926-400-00-020040100000; DN500_PN10=926-500-00-010040100000; DN500_PN16=926-500-00-020040100000; DN600_PN10=926-600-00-010040100000; DN600_PN16=926-600-00-020040100000; DN700_PN10=926-700-00-010020100000; DN700_PN16=926-700-00-020020100000; DN750_PN10=926-750-00-010020100000; DN750_PN16=926-750-00-020020100000; DN800_PN10=926-800-00-010020100000; DN800_PN16=926-800-00-020020100000; DN900_PN10=926-900-00-010020100000; DN900_PN16=926-900-00-020020100000; E=180 mm; FL_R=680 mm; FL_T=40 mm; Hole_R=19 mm  [stored 0.062336 ft]; L=8 mm  [stored 0.0262467 ft]; PCD=1355 mm; Raised_R=664 mm; Raised_dis=5 mm  [stored 0.0164042 ft]; Retainer=40 mm; Rib_R=72 mm; Rib_T=23 mm  [stored 0.0754593 ft]; Rib_shaft=125 mm; Rib_shaft1=96 mm; Seal_R=64 mm; Slot_T=25 mm  [stored 0.082021 ft]; Slot_dim1=16 mm  [stored 0.0524934 ft]; Slt=110 mm; Stem_R=60 mm; Top _Flange_dim1=72 mm; Top _Flange_dim2=66 mm; Top_Flange1=114 mm; Top_Flange_R=208 mm; Top_Flange_R_T=50 mm; Top_Flange_T=75 mm; Top_Rib=72 mm; Wedge=293 mm; bottom_Shaft_R=150 mm; bottom_Shaft_T=24 mm  [stored 0.0787402 ft]; bottom_support_T=144 mm; logo=605 mm; rib_Loctn=48 mm; total_FL_legth=374 mm
- DN1200_PN16: A=381 mm; B=850 mm; Body_T=3 mm  [stored 0.00984252 ft]; Body_end_shaft_R=182 mm; Body_rib_L=120 mm; Body_rib_W=60 mm; Body_shaft_R1=162 mm; Body_shaft_R2=96 mm; Body_shaft_R2_T=114 mm; Body_shaft_R3=125 mm; Body_shaft_R3_T=33 mm  [stored 0.108268 ft]; Bore_R=600 mm; C=1080 mm; D=143 mm; DN=1200 mm; DN080_PN10/16=926-080-00-020140100000; DN1000_PN10=926-A10-00-010020100000; DN1000_PN16=926-A10-00-020020100000; DN100_PN10/16=926-100-00-020140100000; DN1200_PN10=926-A12-00-010020100000; DN1200_PN16=926-A12-00-020020100000; DN1500_PN10=926-A15-00-010020100000; DN1500_PN16=926-A15-00-020020100000; DN150_PN10/16=926-150-00-020040100000; DN1800_PN10=926-A18-00-010020100000; DN1800_PN16=926-A18-00-020020100000; DN200_PN10=926-200-00-010040100000; DN200_PN16=926-200-00-020040100000; DN250_PN10=926-250-00-010040100000; DN250_PN16=926-250-00-020040100000; DN300_PN10=926-300-00-010040100000; DN300_PN16=926-300-00-020040100000; DN350_PN10=926-350-00-010040100000; DN350_PN16=926-350-00-020040100000; DN400_PN10=926-400-00-010040100000; DN400_PN16=926-400-00-020040100000; DN500_PN10=926-500-00-010040100000; DN500_PN16=926-500-00-020040100000; DN600_PN10=926-600-00-010040100000; DN600_PN16=926-600-00-020040100000; DN700_PN10=926-700-00-010020100000; DN700_PN16=926-700-00-020020100000; DN750_PN10=926-750-00-010020100000; DN750_PN16=926-750-00-020020100000; DN800_PN10=926-800-00-010020100000; DN800_PN16=926-800-00-020020100000; DN900_PN10=926-900-00-010020100000; DN900_PN16=926-900-00-020020100000; E=180 mm; FL_R=680 mm; FL_T=50 mm; Hole_R=19 mm  [stored 0.062336 ft]; L=8 mm  [stored 0.0262467 ft]; PCD=1370 mm; Raised_R=664 mm; Raised_dis=5 mm  [stored 0.0164042 ft]; Retainer=40 mm; Rib_R=72 mm; Rib_T=30 mm  [stored 0.0984252 ft]; Rib_shaft=125 mm; Rib_shaft1=96 mm; Seal_R=64 mm; Slot_T=25 mm  [stored 0.082021 ft]; Slot_dim1=16 mm  [stored 0.0524934 ft]; Slt=110 mm; Stem_R=60 mm; Top _Flange_dim1=72 mm; Top _Flange_dim2=66 mm; Top_Flange1=114 mm; Top_Flange_R=208 mm; Top_Flange_R_T=50 mm; Top_Flange_T=143 mm; Top_Rib=72 mm; Wedge=293 mm; bottom_Shaft_R=150 mm; bottom_Shaft_T=24 mm  [stored 0.0787402 ft]; bottom_support_T=144 mm; logo=605 mm; rib_Loctn=48 mm; total_FL_legth=374 mm
- DN1500_PN10: A=381 mm; B=1050 mm; Body_T=3 mm  [stored 0.00984252 ft]; Body_end_shaft_R=182 mm; Body_rib_L=120 mm; Body_rib_W=60 mm; Body_shaft_R1=162 mm; Body_shaft_R2=96 mm; Body_shaft_R2_T=144 mm; Body_shaft_R3=125 mm; Body_shaft_R3_T=33 mm  [stored 0.108268 ft]; Bore_R=750 mm; C=1290 mm; D=180 mm; DN=1500 mm; DN080_PN10/16=926-080-00-020140100000; DN1000_PN10=926-A10-00-010020100000; DN1000_PN16=926-A10-00-020020100000; DN100_PN10/16=926-100-00-020140100000; DN1200_PN10=926-A12-00-010020100000; DN1200_PN16=926-A12-00-020020100000; DN1500_PN10=926-A15-00-010020100000; DN1500_PN16=926-A15-00-020020100000; DN150_PN10/16=926-150-00-020040100000; DN1800_PN10=926-A18-00-010020100000; DN1800_PN16=926-A18-00-020020100000; DN200_PN10=926-200-00-010040100000; DN200_PN16=926-200-00-020040100000; DN250_PN10=926-250-00-010040100000; DN250_PN16=926-250-00-020040100000; DN300_PN10=926-300-00-010040100000; DN300_PN16=926-300-00-020040100000; DN350_PN10=926-350-00-010040100000; DN350_PN16=926-350-00-020040100000; DN400_PN10=926-400-00-010040100000; DN400_PN16=926-400-00-020040100000; DN500_PN10=926-500-00-010040100000; DN500_PN16=926-500-00-020040100000; DN600_PN10=926-600-00-010040100000; DN600_PN16=926-600-00-020040100000; DN700_PN10=926-700-00-010020100000; DN700_PN16=926-700-00-020020100000; DN750_PN10=926-750-00-010020100000; DN750_PN16=926-750-00-020020100000; DN800_PN10=926-800-00-010020100000; DN800_PN16=926-800-00-020020100000; DN900_PN10=926-900-00-010020100000; DN900_PN16=926-900-00-020020100000; E=170 mm; FL_R=820 mm; FL_T=50 mm; Hole_R=25 mm  [stored 0.082021 ft]; L=8 mm  [stored 0.0262467 ft]; PCD=1700 mm; Raised_R=850 mm; Raised_dis=5 mm  [stored 0.0164042 ft]; Retainer=35 mm  [stored 0.114829 ft]; Rib_R=90 mm; Rib_T=30 mm  [stored 0.0984252 ft]; Rib_shaft=125 mm; Rib_shaft1=96 mm; Seal_R=95 mm; Slot_T=27 mm  [stored 0.0885827 ft]; Slot_dim1=16 mm  [stored 0.0524934 ft]; Slt=125 mm; Stem_R=70 mm; Top _Flange_dim1=72 mm; Top _Flange_dim2=66 mm; Top_Flange1=120 mm; Top_Flange_R=238 mm; Top_Flange_R_T=54 mm; Top_Flange_T=143 mm; Top_Rib=90 mm; Wedge=293 mm; bottom_Shaft_R=150 mm; bottom_Shaft_T=24 mm  [stored 0.0787402 ft]; bottom_support_T=144 mm; logo=755 mm; rib_Loctn=48 mm; total_FL_legth=374 mm
- DN1500_PN16: A=381 mm; B=1050 mm; Body_T=3 mm  [stored 0.00984252 ft]; Body_end_shaft_R=182 mm; Body_rib_L=120 mm; Body_rib_W=60 mm; Body_shaft_R1=162 mm; Body_shaft_R2=96 mm; Body_shaft_R2_T=144 mm; Body_shaft_R3=125 mm; Body_shaft_R3_T=33 mm  [stored 0.108268 ft]; Bore_R=750 mm; C=1290 mm; D=180 mm; DN=1500 mm; DN080_PN10/16=926-080-00-020140100000; DN1000_PN10=926-A10-00-010020100000; DN1000_PN16=926-A10-00-020020100000; DN100_PN10/16=926-100-00-020140100000; DN1200_PN10=926-A12-00-010020100000; DN1200_PN16=926-A12-00-020020100000; DN1500_PN10=926-A15-00-010020100000; DN1500_PN16=926-A15-00-020020100000; DN150_PN10/16=926-150-00-020040100000; DN1800_PN10=926-A18-00-010020100000; DN1800_PN16=926-A18-00-020020100000; DN200_PN10=926-200-00-010040100000; DN200_PN16=926-200-00-020040100000; DN250_PN10=926-250-00-010040100000; DN250_PN16=926-250-00-020040100000; DN300_PN10=926-300-00-010040100000; DN300_PN16=926-300-00-020040100000; DN350_PN10=926-350-00-010040100000; DN350_PN16=926-350-00-020040100000; DN400_PN10=926-400-00-010040100000; DN400_PN16=926-400-00-020040100000; DN500_PN10=926-500-00-010040100000; DN500_PN16=926-500-00-020040100000; DN600_PN10=926-600-00-010040100000; DN600_PN16=926-600-00-020040100000; DN700_PN10=926-700-00-010020100000; DN700_PN16=926-700-00-020020100000; DN750_PN10=926-750-00-010020100000; DN750_PN16=926-750-00-020020100000; DN800_PN10=926-800-00-010020100000; DN800_PN16=926-800-00-020020100000; DN900_PN10=926-900-00-010020100000; DN900_PN16=926-900-00-020020100000; E=170 mm; FL_R=820 mm; FL_T=50 mm; Hole_R=28 mm  [stored 0.0918635 ft]; L=8 mm  [stored 0.0262467 ft]; PCD=1700 mm; Raised_R=850 mm; Raised_dis=5 mm  [stored 0.0164042 ft]; Retainer=35 mm  [stored 0.114829 ft]; Rib_R=90 mm; Rib_T=30 mm  [stored 0.0984252 ft]; Rib_shaft=125 mm; Rib_shaft1=96 mm; Seal_R=95 mm; Slot_T=27 mm  [stored 0.0885827 ft]; Slot_dim1=16 mm  [stored 0.0524934 ft]; Slt=125 mm; Stem_R=70 mm; Top _Flange_dim1=72 mm; Top _Flange_dim2=66 mm; Top_Flange1=120 mm; Top_Flange_R=238 mm; Top_Flange_R_T=54 mm; Top_Flange_T=140 mm; Top_Rib=90 mm; Wedge=293 mm; bottom_Shaft_R=150 mm; bottom_Shaft_T=24 mm  [stored 0.0787402 ft]; bottom_support_T=144 mm; logo=755 mm; rib_Loctn=48 mm; total_FL_legth=374 mm
- DN1800_PN10: A=467 mm; B=1230 mm; Body_T=3 mm  [stored 0.00984252 ft]; Body_end_shaft_R=225 mm; Body_rib_L=120 mm; Body_rib_W=15 mm  [stored 0.0492126 ft]; Body_shaft_R1=202 mm; Body_shaft_R2=96 mm; Body_shaft_R2_T=176 mm; Body_shaft_R3=125 mm; Body_shaft_R3_T=33 mm  [stored 0.108268 ft]; Bore_R=900 mm; C=1430 mm; D=220 mm; DN=1800 mm; DN080_PN10/16=926-080-00-020140100000; DN1000_PN10=926-A10-00-010020100000; DN1000_PN16=926-A10-00-020020100000; DN100_PN10/16=926-100-00-020140100000; DN1200_PN10=926-A12-00-010020100000; DN1200_PN16=926-A12-00-020020100000; DN1500_PN10=926-A15-00-010020100000; DN1500_PN16=926-A15-00-020020100000; DN150_PN10/16=926-150-00-020040100000; DN1800_PN10=926-A18-00-010020100000; DN1800_PN16=926-A18-00-020020100000; DN200_PN10=926-200-00-010040100000; DN200_PN16=926-200-00-020040100000; DN250_PN10=926-250-00-010040100000; DN250_PN16=926-250-00-020040100000; DN300_PN10=926-300-00-010040100000; DN300_PN16=926-300-00-020040100000; DN350_PN10=926-350-00-010040100000; DN350_PN16=926-350-00-020040100000; DN400_PN10=926-400-00-010040100000; DN400_PN16=926-400-00-020040100000; DN500_PN10=926-500-00-010040100000; DN500_PN16=926-500-00-020040100000; DN600_PN10=926-600-00-010040100000; DN600_PN16=926-600-00-020040100000; DN700_PN10=926-700-00-010020100000; DN700_PN16=926-700-00-020020100000; DN750_PN10=926-750-00-010020100000; DN750_PN16=926-750-00-020020100000; DN800_PN10=926-800-00-010020100000; DN800_PN16=926-800-00-020020100000; DN900_PN10=926-900-00-010020100000; DN900_PN16=926-900-00-020020100000; E=150 mm; FL_R=1000 mm; FL_T=55 mm; Hole_R=25 mm  [stored 0.082021 ft]; L=8 mm  [stored 0.0262467 ft]; PCD=2020 mm; Raised_R=975 mm; Raised_dis=5 mm  [stored 0.0164042 ft]; Retainer=50 mm; Rib_R=110 mm; Rib_T=33 mm  [stored 0.108268 ft]; Rib_shaft=125 mm; Rib_shaft1=96 mm; Seal_R=79 mm; Slot_T=29 mm  [stored 0.0951444 ft]; Slot_dim1=16 mm  [stored 0.0524934 ft]; Slt=100 mm; Stem_R=70 mm; Top _Flange_dim1=72 mm; Top _Flange_dim2=66 mm; Top_Flange1=140 mm; Top_Flange_R=280 mm; Top_Flange_R_T=58 mm; Top_Flange_T=140 mm; Top_Rib=110 mm; Wedge=359 mm; bottom_Shaft_R=150 mm; bottom_Shaft_T=6 mm  [stored 0.019685 ft]; bottom_support_T=144 mm; logo=905 mm; rib_Loctn=48 mm; total_FL_legth=460 mm
- DN1800_PN16: A=467 mm; B=1230 mm; Body_T=3 mm  [stored 0.00984252 ft]; Body_end_shaft_R=225 mm; Body_rib_L=120 mm; Body_rib_W=15 mm  [stored 0.0492126 ft]; Body_shaft_R1=202 mm; Body_shaft_R2=96 mm; Body_shaft_R2_T=176 mm; Body_shaft_R3=125 mm; Body_shaft_R3_T=33 mm  [stored 0.108268 ft]; Bore_R=900 mm; C=1430 mm; D=220 mm; DN=1800 mm; DN080_PN10/16=926-080-00-020140100000; DN1000_PN10=926-A10-00-010020100000; DN1000_PN16=926-A10-00-020020100000; DN100_PN10/16=926-100-00-020140100000; DN1200_PN10=926-A12-00-010020100000; DN1200_PN16=926-A12-00-020020100000; DN1500_PN10=926-A15-00-010020100000; DN1500_PN16=926-A15-00-020020100000; DN150_PN10/16=926-150-00-020040100000; DN1800_PN10=926-A18-00-010020100000; DN1800_PN16=926-A18-00-020020100000; DN200_PN10=926-200-00-010040100000; DN200_PN16=926-200-00-020040100000; DN250_PN10=926-250-00-010040100000; DN250_PN16=926-250-00-020040100000; DN300_PN10=926-300-00-010040100000; DN300_PN16=926-300-00-020040100000; DN350_PN10=926-350-00-010040100000; DN350_PN16=926-350-00-020040100000; DN400_PN10=926-400-00-010040100000; DN400_PN16=926-400-00-020040100000; DN500_PN10=926-500-00-010040100000; DN500_PN16=926-500-00-020040100000; DN600_PN10=926-600-00-010040100000; DN600_PN16=926-600-00-020040100000; DN700_PN10=926-700-00-010020100000; DN700_PN16=926-700-00-020020100000; DN750_PN10=926-750-00-010020100000; DN750_PN16=926-750-00-020020100000; DN800_PN10=926-800-00-010020100000; DN800_PN16=926-800-00-020020100000; DN900_PN10=926-900-00-010020100000; DN900_PN16=926-900-00-020020100000; E=150 mm; FL_R=1000 mm; FL_T=55 mm; Hole_R=25 mm  [stored 0.082021 ft]; L=8 mm  [stored 0.0262467 ft]; PCD=2020 mm; Raised_R=975 mm; Raised_dis=5 mm  [stored 0.0164042 ft]; Retainer=50 mm; Rib_R=110 mm; Rib_T=33 mm  [stored 0.108268 ft]; Rib_shaft=125 mm; Rib_shaft1=96 mm; Seal_R=79 mm; Slot_T=29 mm  [stored 0.0951444 ft]; Slot_dim1=16 mm  [stored 0.0524934 ft]; Slt=100 mm; Stem_R=70 mm; Top _Flange_dim1=72 mm; Top _Flange_dim2=66 mm; Top_Flange1=140 mm; Top_Flange_R=280 mm; Top_Flange_R_T=58 mm; Top_Flange_T=140 mm; Top_Rib=110 mm; Wedge=359 mm; bottom_Shaft_R=150 mm; bottom_Shaft_T=6 mm  [stored 0.019685 ft]; bottom_support_T=144 mm; logo=905 mm; rib_Loctn=48 mm; total_FL_legth=460 mm
- DN350_PN10: A=203 mm; B=290 mm; Body_T=14 mm  [stored 0.0459318 ft]; Body_end_shaft_R=95 mm; Body_rib_L=67 mm; Body_rib_W=31 mm  [stored 0.101706 ft]; Body_shaft_R1=86 mm; Body_shaft_R2=54 mm; Body_shaft_R2_T=29 mm  [stored 0.0951444 ft]; Body_shaft_R3=70 mm; Body_shaft_R3_T=16 mm  [stored 0.0524934 ft]; Bore_R=175 mm; C=420 mm; D=36 mm  [stored 0.11811 ft]; DN=350 mm; DN080_PN10/16=926-080-00-020140100000; DN1000_PN10=926-A10-00-010020100000; DN1000_PN16=926-A10-00-020020100000; DN100_PN10/16=926-100-00-020140100000; DN1200_PN10=926-A12-00-010020100000; DN1200_PN16=926-A12-00-020020100000; DN1500_PN10=926-A15-00-010020100000; DN1500_PN16=926-A15-00-020020100000; DN150_PN10/16=926-150-00-020040100000; DN1800_PN10=926-A18-00-010020100000; DN1800_PN16=926-A18-00-020020100000; DN200_PN10=926-200-00-010040100000; DN200_PN16=926-200-00-020040100000; DN250_PN10=926-250-00-010040100000; DN250_PN16=926-250-00-020040100000; DN300_PN10=926-300-00-010040100000; DN300_PN16=926-300-00-020040100000; DN350_PN10=926-350-00-010040100000; DN350_PN16=926-350-00-020040100000; DN400_PN10=926-400-00-010040100000; DN400_PN16=926-400-00-020040100000; DN500_PN10=926-500-00-010040100000; DN500_PN16=926-500-00-020040100000; DN600_PN10=926-600-00-010040100000; DN600_PN16=926-600-00-020040100000; DN700_PN10=926-700-00-010020100000; DN700_PN16=926-700-00-020020100000; DN750_PN10=926-750-00-010020100000; DN750_PN16=926-750-00-020020100000; DN800_PN10=926-800-00-010020100000; DN800_PN16=926-800-00-020020100000; DN900_PN10=926-900-00-010020100000; DN900_PN16=926-900-00-020020100000; E=41 mm; FL_R=207 mm; FL_T=25 mm  [stored 0.082021 ft]; Hole_R=12 mm  [stored 0.0393701 ft]; L=6 mm  [stored 0.019685 ft]; PCD=440 mm; Raised_R=215 mm; Raised_dis=4 mm  [stored 0.0131234 ft]; Retainer=16 mm  [stored 0.0524934 ft]; Rib_R=18 mm  [stored 0.0590551 ft]; Rib_T=14 mm  [stored 0.0459318 ft]; Rib_shaft=70 mm; Rib_shaft1=45 mm; Seal_R=16 mm  [stored 0.0524934 ft]; Slot_T=22 mm  [stored 0.0721785 ft]; Slot_dim1=7 mm  [stored 0.0229659 ft]; Slt=36 mm  [stored 0.11811 ft]; Stem_R=27 mm  [stored 0.0885827 ft]; Top _Flange_dim1=40 mm; Top _Flange_dim2=32 mm  [stored 0.104987 ft]; Top_Flange1=29 mm  [stored 0.0951444 ft]; Top_Flange_R=75 mm; Top_Flange_R_T=44 mm; Top_Flange_T=29 mm  [stored 0.0951444 ft]; Top_Rib=18 mm  [stored 0.0590551 ft]; Wedge=156 mm; bottom_Shaft_R=84 mm; bottom_Shaft_T=12 mm  [stored 0.0393701 ft]; bottom_support_T=80 mm; logo=191 mm; rib_Loctn=27 mm  [stored 0.0885827 ft]; total_FL_legth=197 mm
- DN350_PN16: A=203 mm; B=290 mm; Body_T=14 mm  [stored 0.0459318 ft]; Body_end_shaft_R=95 mm; Body_rib_L=67 mm; Body_rib_W=31 mm  [stored 0.101706 ft]; Body_shaft_R1=85 mm; Body_shaft_R2=54 mm; Body_shaft_R2_T=29 mm  [stored 0.0951444 ft]; Body_shaft_R3=70 mm; Body_shaft_R3_T=16 mm  [stored 0.0524934 ft]; Bore_R=175 mm; C=420 mm; D=36 mm  [stored 0.11811 ft]; DN=350 mm; DN080_PN10/16=926-080-00-020140100000; DN1000_PN10=926-A10-00-010020100000; DN1000_PN16=926-A10-00-020020100000; DN100_PN10/16=926-100-00-020140100000; DN1200_PN10=926-A12-00-010020100000; DN1200_PN16=926-A12-00-020020100000; DN1500_PN10=926-A15-00-010020100000; DN1500_PN16=926-A15-00-020020100000; DN150_PN10/16=926-150-00-020040100000; DN1800_PN10=926-A18-00-010020100000; DN1800_PN16=926-A18-00-020020100000; DN200_PN10=926-200-00-010040100000; DN200_PN16=926-200-00-020040100000; DN250_PN10=926-250-00-010040100000; DN250_PN16=926-250-00-020040100000; DN300_PN10=926-300-00-010040100000; DN300_PN16=926-300-00-020040100000; DN350_PN10=926-350-00-010040100000; DN350_PN16=926-350-00-020040100000; DN400_PN10=926-400-00-010040100000; DN400_PN16=926-400-00-020040100000; DN500_PN10=926-500-00-010040100000; DN500_PN16=926-500-00-020040100000; DN600_PN10=926-600-00-010040100000; DN600_PN16=926-600-00-020040100000; DN700_PN10=926-700-00-010020100000; DN700_PN16=926-700-00-020020100000; DN750_PN10=926-750-00-010020100000; DN750_PN16=926-750-00-020020100000; DN800_PN10=926-800-00-010020100000; DN800_PN16=926-800-00-020020100000; DN900_PN10=926-900-00-010020100000; DN900_PN16=926-900-00-020020100000; E=41 mm; FL_R=212 mm; FL_T=27 mm  [stored 0.0885827 ft]; Hole_R=13 mm  [stored 0.0426509 ft]; L=6 mm  [stored 0.019685 ft]; PCD=440 mm; Raised_R=215 mm; Raised_dis=4 mm  [stored 0.0131234 ft]; Retainer=18 mm  [stored 0.0590551 ft]; Rib_R=18 mm  [stored 0.0590551 ft]; Rib_T=15 mm  [stored 0.0492126 ft]; Rib_shaft=60 mm; Rib_shaft1=45 mm; Seal_R=18 mm  [stored 0.0590551 ft]; Slot_T=22 mm  [stored 0.0721785 ft]; Slot_dim1=7 mm  [stored 0.0229659 ft]; Slt=36 mm  [stored 0.11811 ft]; Stem_R=27 mm  [stored 0.0885827 ft]; Top _Flange_dim1=40 mm; Top _Flange_dim2=32 mm  [stored 0.104987 ft]; Top_Flange1=29 mm  [stored 0.0951444 ft]; Top_Flange_R=75 mm; Top_Flange_R_T=44 mm; Top_Flange_T=29 mm  [stored 0.0951444 ft]; Top_Rib=18 mm  [stored 0.0590551 ft]; Wedge=156 mm; bottom_Shaft_R=84 mm; bottom_Shaft_T=12 mm  [stored 0.0393701 ft]; bottom_support_T=80 mm; logo=191 mm; rib_Loctn=27 mm  [stored 0.0885827 ft]; total_FL_legth=197 mm
- DN500_PN10: A=203 mm; B=380 mm; Body_T=3 mm  [stored 0.00984252 ft]; Body_end_shaft_R=95 mm; Body_rib_L=78 mm; Body_rib_W=41 mm; Body_shaft_R1=86 mm; Body_shaft_R2=62 mm; Body_shaft_R2_T=37 mm; Body_shaft_R3=81 mm; Body_shaft_R3_T=16 mm  [stored 0.0524934 ft]; Bore_R=250 mm; C=511 mm; D=46 mm; DN=500 mm; DN080_PN10/16=926-080-00-020140100000; DN1000_PN10=926-A10-00-010020100000; DN1000_PN16=926-A10-00-020020100000; DN100_PN10/16=926-100-00-020140100000; DN1200_PN10=926-A12-00-010020100000; DN1200_PN16=926-A12-00-020020100000; DN1500_PN10=926-A15-00-010020100000; DN1500_PN16=926-A15-00-020020100000; DN150_PN10/16=926-150-00-020040100000; DN1800_PN10=926-A18-00-010020100000; DN1800_PN16=926-A18-00-020020100000; DN200_PN10=926-200-00-010040100000; DN200_PN16=926-200-00-020040100000; DN250_PN10=926-250-00-010040100000; DN250_PN16=926-250-00-020040100000; DN300_PN10=926-300-00-010040100000; DN300_PN16=926-300-00-020040100000; DN350_PN10=926-350-00-010040100000; DN350_PN16=926-350-00-020040100000; DN400_PN10=926-400-00-010040100000; DN400_PN16=926-400-00-020040100000; DN500_PN10=926-500-00-010040100000; DN500_PN16=926-500-00-020040100000; DN600_PN10=926-600-00-010040100000; DN600_PN16=926-600-00-020040100000; DN700_PN10=926-700-00-010020100000; DN700_PN16=926-700-00-020020100000; DN750_PN10=926-750-00-010020100000; DN750_PN16=926-750-00-020020100000; DN800_PN10=926-800-00-010020100000; DN800_PN16=926-800-00-020020100000; DN900_PN10=926-900-00-010020100000; DN900_PN16=926-900-00-020020100000; E=65 mm; FL_R=275 mm; FL_T=26 mm; Hole_R=14 mm  [stored 0.0459318 ft]; L=6 mm  [stored 0.019685 ft]; PCD=565 mm; Raised_R=265 mm; Raised_dis=4 mm  [stored 0.0131234 ft]; Retainer=13 mm  [stored 0.0426509 ft]; Rib_R=23 mm  [stored 0.0754593 ft]; Rib_T=14 mm  [stored 0.0459318 ft]; Rib_shaft=81 mm; Rib_shaft1=62 mm; Seal_R=13 mm  [stored 0.0426509 ft]; Slot_T=22 mm  [stored 0.0721785 ft]; Slot_dim1=7 mm  [stored 0.0229659 ft]; Slt=46 mm; Stem_R=35 mm  [stored 0.114829 ft]; Top _Flange_dim1=47 mm; Top _Flange_dim2=32 mm  [stored 0.104987 ft]; Top_Flange1=37 mm; Top_Flange_R=105 mm; Top_Flange_R_T=44 mm; Top_Flange_T=37 mm; Top_Rib=23 mm  [stored 0.0754593 ft]; Wedge=156 mm; bottom_Shaft_R=97 mm; bottom_Shaft_T=16 mm  [stored 0.0524934 ft]; bottom_support_T=94 mm; logo=255 mm; rib_Loctn=31 mm  [stored 0.101706 ft]; total_FL_legth=197 mm

note: [stored X ft] marks values corroborated as IEEE doubles in the binary element streams (Revit-internal decimal feet)

## geometry (parser evidence)
native form markers: Sweep x17
no freeform markers — native parametric forms only
